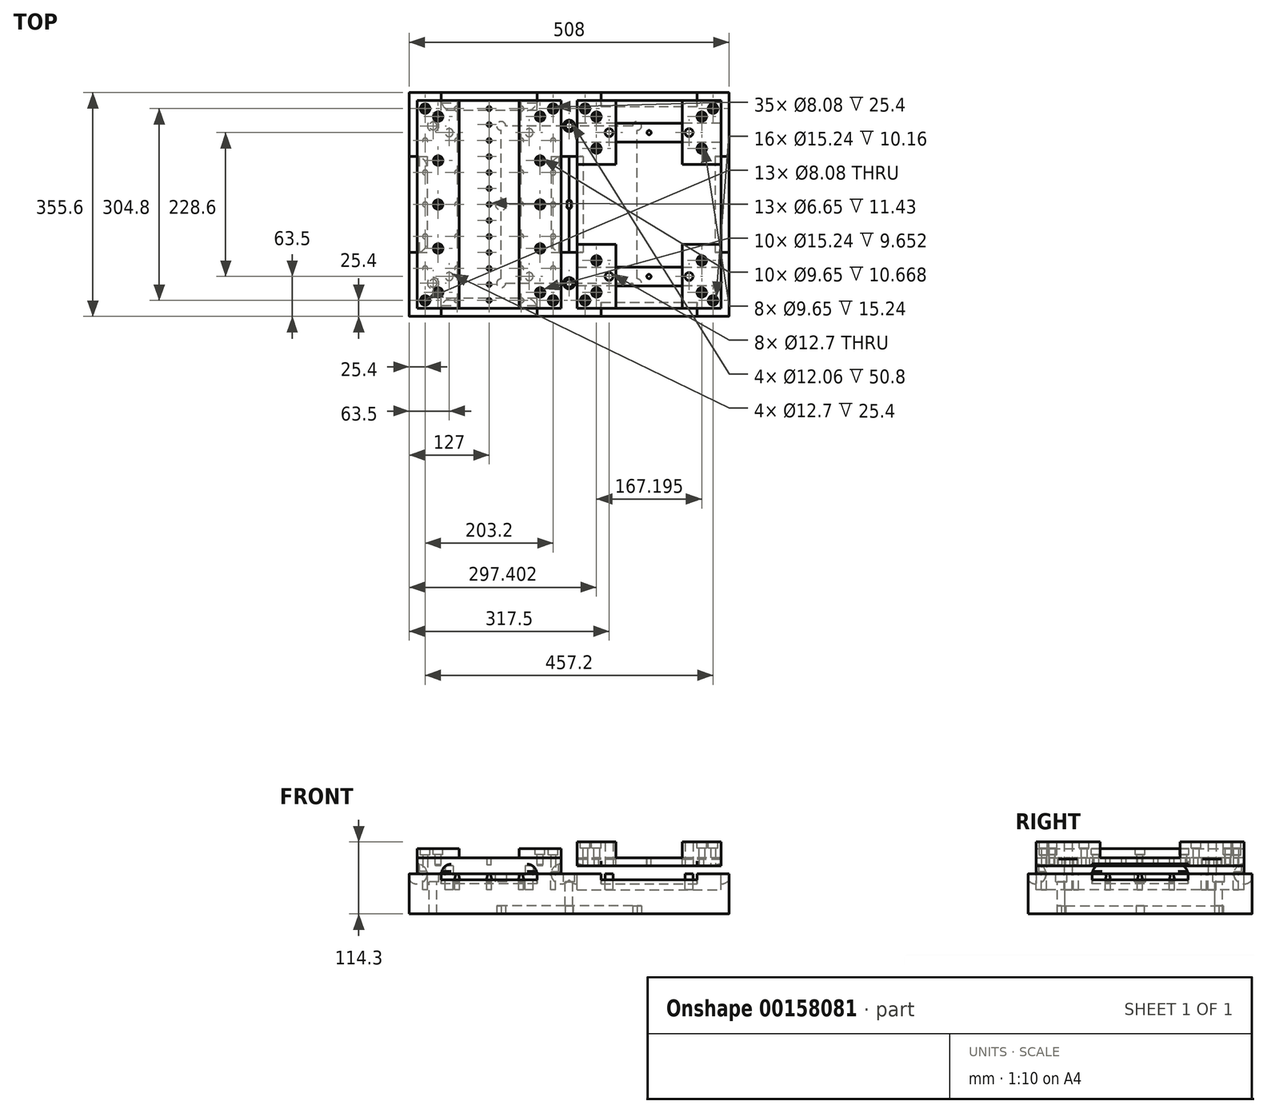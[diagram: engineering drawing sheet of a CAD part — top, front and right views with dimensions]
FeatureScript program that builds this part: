
annotation { "Feature Type Name" : "Feature", "Feature Type Description" : "" }
export const myFeature = defineFeature(function(context is Context, id is Id, definition is map)
    precondition{}
    {
        {
            var Q0;
            Q0=qCreatedBy(makeId("Top.planeOp"),FACE);
            var sketch = newSketch(context, id + "F0", { "sketchPlane" : qUnion([Q0])});
            skLineSegment(sketch, "E0.bottom", {"start": v(253.62, -177.8) * mm, "end": v(-253.62, -177.8) * mm});
            skLineSegment(sketch, "E0.top", {"start": v(253.62, 177.8) * mm, "end": v(-253.62, 177.8) * mm});
            skLineSegment(sketch, "E0.left", {"start": v(254, -177.42) * mm, "end": v(254, 177.42) * mm});
            skLineSegment(sketch, "E0.right", {"start": v(-254, -177.42) * mm, "end": v(-254, 177.42) * mm});
            skPoint(sketch, "E0.middle", {"position": v(0, 0) * mm});
            skPoint(sketch, "E1.visualSharp", {"position": v(-254, 177.8) * mm});
            skArc(sketch, "E1.filletArc", {"start": v(-253.62, 177.8) * mm, "mid": v(-253.89, 177.69) * mm, "end": v(-254, 177.42) * mm});
            skPoint(sketch, "E2.visualSharp", {"position": v(254, 177.8) * mm});
            skArc(sketch, "E2.filletArc", {"start": v(254, 177.42) * mm, "mid": v(253.89, 177.69) * mm, "end": v(253.62, 177.8) * mm});
            skPoint(sketch, "E3.visualSharp", {"position": v(254, -177.8) * mm});
            skArc(sketch, "E3.filletArc", {"start": v(253.62, -177.8) * mm, "mid": v(253.89, -177.69) * mm, "end": v(254, -177.42) * mm});
            skPoint(sketch, "E4.visualSharp", {"position": v(-254, -177.8) * mm});
            skArc(sketch, "E4.filletArc", {"start": v(-254, -177.42) * mm, "mid": v(-253.89, -177.69) * mm, "end": v(-253.62, -177.8) * mm});
            skSolve(sketch);
        }
        {
            var Q0;
            Q0 = qSketchRegion(id + "F0", true);
            extrude(context, id + "F1", {"entities" : qUnion([Q0]), "oppositeDirection" : true, "depth" : 63.5 * mm});
        }
        {
            var Q0;
            Q0=makeQuery(id+"F1.opExtrude","CAP_FACE",FACE,{"disambiguationData":[OSD([sQuery(id+"F0.wireOp",EDGE,"E0.bottom"),sQuery(id+"F0.wireOp",EDGE,"E0.top"),sQuery(id+"F0.wireOp",EDGE,"E0.left"),sQuery(id+"F0.wireOp",EDGE,"E0.right")])],"isStart":true});
            var sketch = newSketch(context, id + "F2", { "sketchPlane" : qUnion([Q0])});
            skLineSegment(sketch, "E5", {"start": v(254, 0) * mm, "end": v(-254, 0) * mm});
            skLineSegment(sketch, "E6", {"start": v(0, 0) * mm, "end": v(0, -125) * mm});
            skLineSegment(sketch, "E7", {"start": v(254, -125) * mm, "end": v(-254, -125) * mm});
            skLineSegment(sketch, "E8.MirrorCS", {"start": v(-254, 0) * mm, "end": v(254, 0) * mm});
            skLineSegment(sketch, "E9.MirrorCS", {"start": v(0, 0) * mm, "end": v(0, 125) * mm});
            skLineSegment(sketch, "E10", {"start": v(254, 125) * mm, "end": v(-254, 125) * mm});
            skLineSegment(sketch, "E11", {"start": v(254, -125) * mm, "end": v(215.9, -125) * mm});
            skLineSegment(sketch, "E12", {"start": v(254, 0) * mm, "end": v(215.9, 0) * mm});
            skLineSegment(sketch, "E13", {"start": v(254, 125) * mm, "end": v(215.9, 125) * mm});
            skLineSegment(sketch, "E14", {"start": v(215.9, 0) * mm, "end": v(0, 0) * mm});
            skLineSegment(sketch, "E15", {"start": v(0, 0) * mm, "end": v(-215.9, 0) * mm});
            skCircle(sketch, "E16", {"center": v(215.9, -125) * mm, "radius": 6.03 * mm});
            skCircle(sketch, "E17", {"center": v(215.9, 125) * mm, "radius": 6.03 * mm});
            skCircle(sketch, "E18.1.0.0", {"center": v(0, 125) * mm, "radius": 6.03 * mm});
            skCircle(sketch, "E18.1.0.1", {"center": v(0, -125) * mm, "radius": 6.03 * mm});
            skCircle(sketch, "E18.2.0.0", {"center": v(-215.9, 125) * mm, "radius": 6.03 * mm});
            skCircle(sketch, "E18.2.0.1", {"center": v(-215.9, -125) * mm, "radius": 6.03 * mm});
            skLineSegment(sketch, "E18.direction1", {"start": v(215.9, 125) * mm, "end": v(0, 125) * mm, "construction": true});
            skCircle(sketch, "E19", {"center": v(107.95, 0) * mm, "radius": 6.03 * mm});
            skCircle(sketch, "E20", {"center": v(-107.95, 0) * mm, "radius": 6.03 * mm});
            skCircle(sketch, "E21", {"center": v(0, 0) * mm, "radius": 6.35 * mm});
            skSolve(sketch);
        }
        {
            var Q0;
            {var subQ0=sQuery(id+"F2.wireOp",EDGE,"E11");var subQ1=sQuery(id+"F2.wireOp",EDGE,"E7");var subQ2=makeQuery(id+"F2.imprint","INTERSECT",VERTEX,{"derivedFrom":[subQ1,subQ0]});Q0=makeQuery(id+"F2.imprint","IMPRINT",FACE,{"disambiguationData":[TD([[makeQuery(id+"F2.imprint","IMPRINT",EDGE,{"disambiguationData":[TD([[subQ2,-1.0]])],"derivedFrom":subQ1}),-1.0]])]});}
            var Q1;
            {var subQ0=sQuery(id+"F2.wireOp",EDGE,"E11");var subQ1=sQuery(id+"F2.wireOp",EDGE,"E7");var subQ2=makeQuery(id+"F2.imprint","INTERSECT",VERTEX,{"derivedFrom":[subQ1,subQ0]});Q1=makeQuery(id+"F2.imprint","IMPRINT",FACE,{"disambiguationData":[TD([[makeQuery(id+"F2.imprint","IMPRINT",EDGE,{"disambiguationData":[TD([[subQ2,-1.0]])],"derivedFrom":subQ1}),1.0]])]});}
            var Q2;
            {var subQ0=sQuery(id+"F2.wireOp",EDGE,"E18.2.0.1");var subQ1=sQuery(id+"F2.wireOp",EDGE,"E7");var subQ2=makeQuery(id+"F2.imprint","INTERSECT",VERTEX,{"disambiguationData":[OD(0.0)],"derivedFrom":[subQ1,subQ0]});Q2=makeQuery(id+"F2.imprint","IMPRINT",FACE,{"disambiguationData":[TD([[makeQuery(id+"F2.imprint","IMPRINT",EDGE,{"disambiguationData":[TD([[subQ2,-1.0]])],"derivedFrom":subQ1}),-1.0]])]});}
            var Q3;
            {var subQ0=sQuery(id+"F2.wireOp",EDGE,"E18.2.0.1");var subQ1=sQuery(id+"F2.wireOp",EDGE,"E7");var subQ2=makeQuery(id+"F2.imprint","INTERSECT",VERTEX,{"disambiguationData":[OD(0.0)],"derivedFrom":[subQ1,subQ0]});Q3=makeQuery(id+"F2.imprint","IMPRINT",FACE,{"disambiguationData":[TD([[makeQuery(id+"F2.imprint","IMPRINT",EDGE,{"disambiguationData":[TD([[subQ2,-1.0]])],"derivedFrom":subQ1}),1.0]])]});}
            var Q4;
            {var subQ0=sQuery(id+"F2.wireOp",EDGE,"E13");var subQ1=sQuery(id+"F2.wireOp",EDGE,"E10");var subQ2=makeQuery(id+"F2.imprint","INTERSECT",VERTEX,{"derivedFrom":[subQ1,subQ0]});Q4=makeQuery(id+"F2.imprint","IMPRINT",FACE,{"disambiguationData":[TD([[makeQuery(id+"F2.imprint","IMPRINT",EDGE,{"disambiguationData":[TD([[subQ2,-1.0]])],"derivedFrom":subQ1}),-1.0]])]});}
            var Q5;
            {var subQ0=sQuery(id+"F2.wireOp",EDGE,"E13");var subQ1=sQuery(id+"F2.wireOp",EDGE,"E10");var subQ2=makeQuery(id+"F2.imprint","INTERSECT",VERTEX,{"derivedFrom":[subQ1,subQ0]});Q5=makeQuery(id+"F2.imprint","IMPRINT",FACE,{"disambiguationData":[TD([[makeQuery(id+"F2.imprint","IMPRINT",EDGE,{"disambiguationData":[TD([[subQ2,-1.0]])],"derivedFrom":subQ1}),1.0]])]});}
            var Q6;
            {var subQ0=sQuery(id+"F2.wireOp",EDGE,"E18.2.0.0");var subQ1=sQuery(id+"F2.wireOp",EDGE,"E10");var subQ2=makeQuery(id+"F2.imprint","INTERSECT",VERTEX,{"disambiguationData":[OD(0.0)],"derivedFrom":[subQ1,subQ0]});Q6=makeQuery(id+"F2.imprint","IMPRINT",FACE,{"disambiguationData":[TD([[makeQuery(id+"F2.imprint","IMPRINT",EDGE,{"disambiguationData":[TD([[subQ2,-1.0]])],"derivedFrom":subQ1}),-1.0]])]});}
            var Q7;
            {var subQ0=sQuery(id+"F2.wireOp",EDGE,"E18.2.0.0");var subQ1=sQuery(id+"F2.wireOp",EDGE,"E10");var subQ2=makeQuery(id+"F2.imprint","INTERSECT",VERTEX,{"disambiguationData":[OD(0.0)],"derivedFrom":[subQ1,subQ0]});Q7=makeQuery(id+"F2.imprint","IMPRINT",FACE,{"disambiguationData":[TD([[makeQuery(id+"F2.imprint","IMPRINT",EDGE,{"disambiguationData":[TD([[subQ2,-1.0]])],"derivedFrom":subQ1}),1.0]])]});}
            var Q8;
            {var subQ0=sQuery(id+"F2.wireOp",EDGE,"E19");var subQ1=sQuery(id+"F2.wireOp",EDGE,"E14");var subQ2=makeQuery(id+"F2.imprint","INTERSECT",VERTEX,{"disambiguationData":[OD(0.0)],"derivedFrom":[subQ1,subQ0]});Q8=makeQuery(id+"F2.imprint","IMPRINT",FACE,{"disambiguationData":[TD([[makeQuery(id+"F2.imprint","IMPRINT",EDGE,{"disambiguationData":[TD([[subQ2,-1.0]])],"derivedFrom":subQ1}),-1.0]])]});}
            var Q9;
            {var subQ0=sQuery(id+"F2.wireOp",EDGE,"E19");var subQ1=sQuery(id+"F2.wireOp",EDGE,"E14");var subQ2=makeQuery(id+"F2.imprint","INTERSECT",VERTEX,{"disambiguationData":[OD(0.0)],"derivedFrom":[subQ1,subQ0]});Q9=makeQuery(id+"F2.imprint","IMPRINT",FACE,{"disambiguationData":[TD([[makeQuery(id+"F2.imprint","IMPRINT",EDGE,{"disambiguationData":[TD([[subQ2,-1.0]])],"derivedFrom":subQ1}),1.0]])]});}
            var Q10;
            {var subQ0=sQuery(id+"F2.wireOp",EDGE,"E20");var subQ1=sQuery(id+"F2.wireOp",EDGE,"E15");var subQ2=makeQuery(id+"F2.imprint","INTERSECT",VERTEX,{"disambiguationData":[OD(0.0)],"derivedFrom":[subQ1,subQ0]});Q10=makeQuery(id+"F2.imprint","IMPRINT",FACE,{"disambiguationData":[TD([[makeQuery(id+"F2.imprint","IMPRINT",EDGE,{"disambiguationData":[TD([[subQ2,-1.0]])],"derivedFrom":subQ1}),-1.0]])]});}
            var Q11;
            {var subQ0=sQuery(id+"F2.wireOp",EDGE,"E20");var subQ1=sQuery(id+"F2.wireOp",EDGE,"E15");var subQ2=makeQuery(id+"F2.imprint","INTERSECT",VERTEX,{"disambiguationData":[OD(0.0)],"derivedFrom":[subQ1,subQ0]});Q11=makeQuery(id+"F2.imprint","IMPRINT",FACE,{"disambiguationData":[TD([[makeQuery(id+"F2.imprint","IMPRINT",EDGE,{"disambiguationData":[TD([[subQ2,-1.0]])],"derivedFrom":subQ1}),1.0]])]});}
            var Q12;
            {var subQ0=sQuery(id+"F2.wireOp",EDGE,"E7");var subQ1=sQuery(id+"F2.wireOp",EDGE,"E6");var subQ2=makeQuery(id+"F2.imprint","INTERSECT",VERTEX,{"derivedFrom":[subQ1,subQ0]});Q12=makeQuery(id+"F2.imprint","IMPRINT",FACE,{"disambiguationData":[TD([[makeQuery(id+"F2.imprint","IMPRINT",EDGE,{"disambiguationData":[TD([[subQ2,1.0]])],"derivedFrom":subQ1}),1.0]])]});}
            var Q13;
            {var subQ0=sQuery(id+"F2.wireOp",EDGE,"E7");var subQ1=sQuery(id+"F2.wireOp",EDGE,"E6");var subQ2=makeQuery(id+"F2.imprint","INTERSECT",VERTEX,{"derivedFrom":[subQ1,subQ0]});Q13=makeQuery(id+"F2.imprint","IMPRINT",FACE,{"disambiguationData":[TD([[makeQuery(id+"F2.imprint","IMPRINT",EDGE,{"disambiguationData":[TD([[subQ2,1.0]])],"derivedFrom":subQ1}),-1.0]])]});}
            var Q14;
            {var subQ0=sQuery(id+"F2.wireOp",EDGE,"E7");var subQ1=makeQuery(id+"F2.imprint","INTERSECT",VERTEX,{"derivedFrom":[sQuery(id+"F2.wireOp",EDGE,"E6"),subQ0]});Q14=makeQuery(id+"F2.imprint","IMPRINT",FACE,{"disambiguationData":[TD([[makeQuery(id+"F2.imprint","IMPRINT",EDGE,{"disambiguationData":[TD([[subQ1,1.0]])],"derivedFrom":subQ0}),1.0]])]});}
            var Q15;
            {var subQ0=sQuery(id+"F2.wireOp",EDGE,"E10");var subQ1=sQuery(id+"F2.wireOp",EDGE,"E9.MirrorCS");var subQ2=makeQuery(id+"F2.imprint","INTERSECT",VERTEX,{"derivedFrom":[subQ1,subQ0]});Q15=makeQuery(id+"F2.imprint","IMPRINT",FACE,{"disambiguationData":[TD([[makeQuery(id+"F2.imprint","IMPRINT",EDGE,{"disambiguationData":[TD([[subQ2,1.0]])],"derivedFrom":subQ1}),-1.0]])]});}
            var Q16;
            {var subQ0=sQuery(id+"F2.wireOp",EDGE,"E10");var subQ1=sQuery(id+"F2.wireOp",EDGE,"E9.MirrorCS");var subQ2=makeQuery(id+"F2.imprint","INTERSECT",VERTEX,{"derivedFrom":[subQ1,subQ0]});Q16=makeQuery(id+"F2.imprint","IMPRINT",FACE,{"disambiguationData":[TD([[makeQuery(id+"F2.imprint","IMPRINT",EDGE,{"disambiguationData":[TD([[subQ2,1.0]])],"derivedFrom":subQ1}),1.0]])]});}
            var Q17;
            {var subQ0=sQuery(id+"F2.wireOp",EDGE,"E10");var subQ1=makeQuery(id+"F2.imprint","INTERSECT",VERTEX,{"derivedFrom":[sQuery(id+"F2.wireOp",EDGE,"E9.MirrorCS"),subQ0]});Q17=makeQuery(id+"F2.imprint","IMPRINT",FACE,{"disambiguationData":[TD([[makeQuery(id+"F2.imprint","IMPRINT",EDGE,{"disambiguationData":[TD([[subQ1,1.0]])],"derivedFrom":subQ0}),-1.0]])]});}
            extrude(context, id + "F3", {"entities" : qUnion([Q0, Q1, Q2, Q3, Q4, Q5, Q6, Q7, Q8, Q9, Q10, Q11, Q12, Q13, Q14, Q15, Q16, Q17]), "operationType" : NewBodyOperationType.REMOVE, "oppositeDirection" : true, "depth" : 76.2 * mm});
        }
        {
            var Q0;
            {var subQ1=sQuery(id+"F2.wireOp",EDGE,"E6");var subQ3=sQuery(id+"F2.wireOp",EDGE,"E21");var subQ4=makeQuery(id+"F2.imprint","INTERSECT",VERTEX,{"derivedFrom":[subQ1,subQ3]});Q0=makeQuery(id+"F2.imprint","IMPRINT",FACE,{"disambiguationData":[TD([[makeQuery(id+"F2.imprint","IMPRINT",EDGE,{"disambiguationData":[TD([[subQ4,1.0]])],"derivedFrom":subQ3}),1.0]])]});}
            var Q1;
            {var subQ1=sQuery(id+"F2.wireOp",EDGE,"E6");var subQ3=sQuery(id+"F2.wireOp",EDGE,"E21");var subQ4=makeQuery(id+"F2.imprint","INTERSECT",VERTEX,{"derivedFrom":[subQ1,subQ3]});Q1=makeQuery(id+"F2.imprint","IMPRINT",FACE,{"disambiguationData":[TD([[makeQuery(id+"F2.imprint","IMPRINT",EDGE,{"disambiguationData":[TD([[subQ4,-1.0]])],"derivedFrom":subQ3}),1.0]])]});}
            var Q2;
            {var subQ1=sQuery(id+"F2.wireOp",EDGE,"E9.MirrorCS");var subQ3=sQuery(id+"F2.wireOp",EDGE,"E21");var subQ4=makeQuery(id+"F2.imprint","INTERSECT",VERTEX,{"derivedFrom":[subQ1,subQ3]});Q2=makeQuery(id+"F2.imprint","IMPRINT",FACE,{"disambiguationData":[TD([[makeQuery(id+"F2.imprint","IMPRINT",EDGE,{"disambiguationData":[TD([[subQ4,1.0]])],"derivedFrom":subQ3}),1.0]])]});}
            var Q3;
            {var subQ1=sQuery(id+"F2.wireOp",EDGE,"E9.MirrorCS");var subQ3=sQuery(id+"F2.wireOp",EDGE,"E21");var subQ4=makeQuery(id+"F2.imprint","INTERSECT",VERTEX,{"derivedFrom":[subQ1,subQ3]});Q3=makeQuery(id+"F2.imprint","IMPRINT",FACE,{"disambiguationData":[TD([[makeQuery(id+"F2.imprint","IMPRINT",EDGE,{"disambiguationData":[TD([[subQ4,-1.0]])],"derivedFrom":subQ3}),1.0]])]});}
            extrude(context, id + "F4", {"entities" : qUnion([Q0, Q1, Q2, Q3]), "operationType" : NewBodyOperationType.REMOVE, "oppositeDirection" : true, "depth" : 12.7 * mm});
        }
        {
            var Q0;
            Q0=makeQuery(id+"F1.opExtrude","CAP_FACE",FACE,{"disambiguationData":[OSD([sQuery(id+"F0.wireOp",EDGE,"E0.bottom"),sQuery(id+"F0.wireOp",EDGE,"E0.top"),sQuery(id+"F0.wireOp",EDGE,"E0.left"),sQuery(id+"F0.wireOp",EDGE,"E0.right")])],"isStart":true});
            var sketch = newSketch(context, id + "F5", { "sketchPlane" : qUnion([Q0])});
            skCircle(sketch, "E22", {"center": v(215.9, -125) * mm, "radius": 9.02 * mm});
            skCircle(sketch, "E23", {"center": v(0, -125) * mm, "radius": 9.02 * mm});
            skCircle(sketch, "E24", {"center": v(107.95, 0) * mm, "radius": 9.02 * mm});
            skCircle(sketch, "E25", {"center": v(215.9, 125) * mm, "radius": 9.02 * mm});
            skCircle(sketch, "E26", {"center": v(0, 125) * mm, "radius": 9.02 * mm});
            skCircle(sketch, "E27", {"center": v(-215.9, 125) * mm, "radius": 9.02 * mm});
            skCircle(sketch, "E28", {"center": v(-107.95, 0) * mm, "radius": 9.02 * mm});
            skCircle(sketch, "E29", {"center": v(-215.9, -125) * mm, "radius": 9.02 * mm});
            skSolve(sketch);
        }
        {
            var Q0;
            Q0 = qSketchRegion(id + "F5", true);
            extrude(context, id + "F6", {"entities" : qUnion([Q0]), "operationType" : NewBodyOperationType.REMOVE, "oppositeDirection" : true, "depth" : 12.7 * mm});
        }
        {
            var Q0;
            Q0=makeQuery(id+"F1.opExtrude","CAP_FACE",FACE,{"disambiguationData":[OSD([sQuery(id+"F0.wireOp",EDGE,"E0.bottom"),sQuery(id+"F0.wireOp",EDGE,"E0.top"),sQuery(id+"F0.wireOp",EDGE,"E0.left"),sQuery(id+"F0.wireOp",EDGE,"E0.right"),sQuery(id+"F0.wireOp",EDGE,"E1.filletArc"),sQuery(id+"F0.wireOp",EDGE,"E2.filletArc"),sQuery(id+"F0.wireOp",EDGE,"E3.filletArc"),sQuery(id+"F0.wireOp",EDGE,"E4.filletArc")])],"isStart":false});
            var sketch = newSketch(context, id + "F7", { "sketchPlane" : qUnion([Q0])});
            skLineSegment(sketch, "E30", {"start": v(-215.9, 125) * mm, "end": v(215.9, 125) * mm});
            skLineSegment(sketch, "E31", {"start": v(215.9, 125) * mm, "end": v(215.9, -125) * mm});
            skLineSegment(sketch, "E32", {"start": v(215.9, -125) * mm, "end": v(-215.9, -125) * mm});
            skLineSegment(sketch, "E33", {"start": v(-215.9, -125) * mm, "end": v(-215.9, 125) * mm});
            skLineSegment(sketch, "E34", {"start": v(-215.9, 0) * mm, "end": v(215.9, 0) * mm});
            skLineSegment(sketch, "E35", {"start": v(-107.95, 0) * mm, "end": v(-107.95, 125) * mm});
            skLineSegment(sketch, "E36", {"start": v(-107.95, 0) * mm, "end": v(-107.95, -125) * mm});
            skLineSegment(sketch, "E37", {"start": v(107.95, 0) * mm, "end": v(107.95, 125) * mm});
            skLineSegment(sketch, "E38", {"start": v(107.95, 0) * mm, "end": v(107.95, -125) * mm});
            skCircle(sketch, "E39", {"center": v(-107.95, -125) * mm, "radius": 7 * mm});
            skCircle(sketch, "E40", {"center": v(-107.95, 125) * mm, "radius": 7 * mm});
            skCircle(sketch, "E41", {"center": v(107.95, 125) * mm, "radius": 7 * mm});
            skCircle(sketch, "E42", {"center": v(107.95, -125) * mm, "radius": 7 * mm});
            skCircle(sketch, "E43", {"center": v(0, 0) * mm, "radius": 6.35 * mm});
            skSolve(sketch);
        }
        {
            var Q0;
            {var subQ0=sQuery(id+"F7.wireOp",EDGE,"E30");var subQ1=makeQuery(id+"F7.imprint","INTERSECT",VERTEX,{"derivedFrom":[subQ0,sQuery(id+"F7.wireOp",EDGE,"E35")]});Q0=makeQuery(id+"F7.imprint","IMPRINT",FACE,{"disambiguationData":[TD([[makeQuery(id+"F7.imprint","IMPRINT",EDGE,{"disambiguationData":[TD([[subQ1,1.0]])],"derivedFrom":subQ0}),1.0]])]});}
            var Q1;
            {var subQ0=sQuery(id+"F7.wireOp",EDGE,"E35");var subQ1=sQuery(id+"F7.wireOp",EDGE,"E30");var subQ2=makeQuery(id+"F7.imprint","INTERSECT",VERTEX,{"derivedFrom":[subQ1,subQ0]});Q1=makeQuery(id+"F7.imprint","IMPRINT",FACE,{"disambiguationData":[TD([[makeQuery(id+"F7.imprint","IMPRINT",EDGE,{"disambiguationData":[TD([[subQ2,1.0]])],"derivedFrom":subQ1}),-1.0]])]});}
            var Q2;
            {var subQ0=sQuery(id+"F7.wireOp",EDGE,"E35");var subQ1=sQuery(id+"F7.wireOp",EDGE,"E30");var subQ2=makeQuery(id+"F7.imprint","INTERSECT",VERTEX,{"derivedFrom":[subQ1,subQ0]});Q2=makeQuery(id+"F7.imprint","IMPRINT",FACE,{"disambiguationData":[TD([[makeQuery(id+"F7.imprint","IMPRINT",EDGE,{"disambiguationData":[TD([[subQ2,-1.0]])],"derivedFrom":subQ1}),-1.0]])]});}
            var Q3;
            {var subQ0=sQuery(id+"F7.wireOp",EDGE,"E30");var subQ1=makeQuery(id+"F7.imprint","INTERSECT",VERTEX,{"derivedFrom":[subQ0,sQuery(id+"F7.wireOp",EDGE,"E37")]});Q3=makeQuery(id+"F7.imprint","IMPRINT",FACE,{"disambiguationData":[TD([[makeQuery(id+"F7.imprint","IMPRINT",EDGE,{"disambiguationData":[TD([[subQ1,1.0]])],"derivedFrom":subQ0}),1.0]])]});}
            var Q4;
            {var subQ0=sQuery(id+"F7.wireOp",EDGE,"E37");var subQ1=sQuery(id+"F7.wireOp",EDGE,"E30");var subQ2=makeQuery(id+"F7.imprint","INTERSECT",VERTEX,{"derivedFrom":[subQ1,subQ0]});Q4=makeQuery(id+"F7.imprint","IMPRINT",FACE,{"disambiguationData":[TD([[makeQuery(id+"F7.imprint","IMPRINT",EDGE,{"disambiguationData":[TD([[subQ2,1.0]])],"derivedFrom":subQ1}),-1.0]])]});}
            var Q5;
            {var subQ0=sQuery(id+"F7.wireOp",EDGE,"E37");var subQ1=sQuery(id+"F7.wireOp",EDGE,"E30");var subQ2=makeQuery(id+"F7.imprint","INTERSECT",VERTEX,{"derivedFrom":[subQ1,subQ0]});Q5=makeQuery(id+"F7.imprint","IMPRINT",FACE,{"disambiguationData":[TD([[makeQuery(id+"F7.imprint","IMPRINT",EDGE,{"disambiguationData":[TD([[subQ2,-1.0]])],"derivedFrom":subQ1}),-1.0]])]});}
            var Q6;
            {var subQ0=sQuery(id+"F7.wireOp",EDGE,"E32");var subQ1=makeQuery(id+"F7.imprint","INTERSECT",VERTEX,{"derivedFrom":[subQ0,sQuery(id+"F7.wireOp",EDGE,"E38")]});Q6=makeQuery(id+"F7.imprint","IMPRINT",FACE,{"disambiguationData":[TD([[makeQuery(id+"F7.imprint","IMPRINT",EDGE,{"disambiguationData":[TD([[subQ1,1.0]])],"derivedFrom":subQ0}),1.0]])]});}
            var Q7;
            {var subQ0=sQuery(id+"F7.wireOp",EDGE,"E38");var subQ1=sQuery(id+"F7.wireOp",EDGE,"E32");var subQ2=makeQuery(id+"F7.imprint","INTERSECT",VERTEX,{"derivedFrom":[subQ1,subQ0]});Q7=makeQuery(id+"F7.imprint","IMPRINT",FACE,{"disambiguationData":[TD([[makeQuery(id+"F7.imprint","IMPRINT",EDGE,{"disambiguationData":[TD([[subQ2,-1.0]])],"derivedFrom":subQ1}),-1.0]])]});}
            var Q8;
            {var subQ0=sQuery(id+"F7.wireOp",EDGE,"E38");var subQ1=sQuery(id+"F7.wireOp",EDGE,"E32");var subQ2=makeQuery(id+"F7.imprint","INTERSECT",VERTEX,{"derivedFrom":[subQ1,subQ0]});Q8=makeQuery(id+"F7.imprint","IMPRINT",FACE,{"disambiguationData":[TD([[makeQuery(id+"F7.imprint","IMPRINT",EDGE,{"disambiguationData":[TD([[subQ2,1.0]])],"derivedFrom":subQ1}),-1.0]])]});}
            var Q9;
            {var subQ0=sQuery(id+"F7.wireOp",EDGE,"E36");var subQ1=sQuery(id+"F7.wireOp",EDGE,"E32");var subQ2=makeQuery(id+"F7.imprint","INTERSECT",VERTEX,{"derivedFrom":[subQ1,subQ0]});Q9=makeQuery(id+"F7.imprint","IMPRINT",FACE,{"disambiguationData":[TD([[makeQuery(id+"F7.imprint","IMPRINT",EDGE,{"disambiguationData":[TD([[subQ2,-1.0]])],"derivedFrom":subQ1}),-1.0]])]});}
            var Q10;
            {var subQ0=sQuery(id+"F7.wireOp",EDGE,"E36");var subQ1=sQuery(id+"F7.wireOp",EDGE,"E32");var subQ2=makeQuery(id+"F7.imprint","INTERSECT",VERTEX,{"derivedFrom":[subQ1,subQ0]});Q10=makeQuery(id+"F7.imprint","IMPRINT",FACE,{"disambiguationData":[TD([[makeQuery(id+"F7.imprint","IMPRINT",EDGE,{"disambiguationData":[TD([[subQ2,1.0]])],"derivedFrom":subQ1}),-1.0]])]});}
            var Q11;
            {var subQ0=sQuery(id+"F7.wireOp",EDGE,"E32");var subQ1=makeQuery(id+"F7.imprint","INTERSECT",VERTEX,{"derivedFrom":[subQ0,sQuery(id+"F7.wireOp",EDGE,"E36")]});Q11=makeQuery(id+"F7.imprint","IMPRINT",FACE,{"disambiguationData":[TD([[makeQuery(id+"F7.imprint","IMPRINT",EDGE,{"disambiguationData":[TD([[subQ1,1.0]])],"derivedFrom":subQ0}),1.0]])]});}
            var Q12;
            {var subQ0=sQuery(id+"F7.wireOp",EDGE,"E43");var subQ1=sQuery(id+"F7.wireOp",EDGE,"E34");var subQ2=makeQuery(id+"F7.imprint","INTERSECT",VERTEX,{"disambiguationData":[OD(0.0)],"derivedFrom":[subQ1,subQ0]});Q12=makeQuery(id+"F7.imprint","IMPRINT",FACE,{"disambiguationData":[TD([[makeQuery(id+"F7.imprint","IMPRINT",EDGE,{"disambiguationData":[TD([[subQ2,-1.0]])],"derivedFrom":subQ1}),-1.0]])]});}
            var Q13;
            {var subQ0=sQuery(id+"F7.wireOp",EDGE,"E43");var subQ1=sQuery(id+"F7.wireOp",EDGE,"E34");var subQ2=makeQuery(id+"F7.imprint","INTERSECT",VERTEX,{"disambiguationData":[OD(0.0)],"derivedFrom":[subQ1,subQ0]});Q13=makeQuery(id+"F7.imprint","IMPRINT",FACE,{"disambiguationData":[TD([[makeQuery(id+"F7.imprint","IMPRINT",EDGE,{"disambiguationData":[TD([[subQ2,-1.0]])],"derivedFrom":subQ1}),1.0]])]});}
            extrude(context, id + "F8", {"entities" : qUnion([Q0, Q1, Q2, Q3, Q4, Q5, Q6, Q7, Q8, Q9, Q10, Q11, Q12, Q13]), "operationType" : NewBodyOperationType.REMOVE, "oppositeDirection" : true, "depth" : 12.7 * mm});
        }
        {
            var Q0;
            Q0=makeQuery(id+"F0.imprint","IMPRINT",FACE,{"disambiguationData":[TD([[makeQuery(id+"F0.imprint","IMPRINT",EDGE,{"derivedFrom":sQuery(id+"F0.wireOp",EDGE,"E0.bottom")}),-1.0]])]});
            var sketch = newSketch(context, id + "F9", { "sketchPlane" : qUnion([Q0])});
            skLineSegment(sketch, "E44", {"start": v(0, 0) * mm, "end": v(-254, 0) * mm});
            skLineSegment(sketch, "E45", {"start": v(-254, 177.8) * mm, "end": v(-254, 0) * mm});
            skLineSegment(sketch, "E46", {"start": v(-254, 177.8) * mm, "end": v(-228.6, 177.8) * mm});
            skLineSegment(sketch, "E47", {"start": v(-228.6, 177.8) * mm, "end": v(-228.6, 152.4) * mm});
            skCircle(sketch, "E48", {"center": v(-228.6, 152.4) * mm, "radius": 4.04 * mm});
            skCircle(sketch, "E49.0.1.0", {"center": v(-228.6, 101.6) * mm, "radius": 4.04 * mm});
            skCircle(sketch, "E49.0.2.0", {"center": v(-228.6, 50.8) * mm, "radius": 4.04 * mm});
            skCircle(sketch, "E49.0.3.0", {"center": v(-228.6, 0) * mm, "radius": 4.04 * mm});
            skCircle(sketch, "E49.0.4.0", {"center": v(-228.6, -50.8) * mm, "radius": 4.04 * mm});
            skCircle(sketch, "E49.0.5.0", {"center": v(-228.6, -101.6) * mm, "radius": 4.04 * mm});
            skCircle(sketch, "E49.0.6.0", {"center": v(-228.6, -152.4) * mm, "radius": 4.04 * mm});
            skCircle(sketch, "E49.1.0.0", {"center": v(-177.8, 152.4) * mm, "radius": 4.04 * mm});
            skCircle(sketch, "E49.1.1.0", {"center": v(-177.8, 101.6) * mm, "radius": 4.04 * mm});
            skCircle(sketch, "E49.1.2.0", {"center": v(-177.8, 50.8) * mm, "radius": 4.04 * mm});
            skCircle(sketch, "E49.1.3.0", {"center": v(-177.8, 0) * mm, "radius": 4.04 * mm});
            skCircle(sketch, "E49.1.4.0", {"center": v(-177.8, -50.8) * mm, "radius": 4.04 * mm});
            skCircle(sketch, "E49.1.5.0", {"center": v(-177.8, -101.6) * mm, "radius": 4.04 * mm});
            skCircle(sketch, "E49.1.6.0", {"center": v(-177.8, -152.4) * mm, "radius": 4.04 * mm});
            skCircle(sketch, "E49.2.0.0", {"center": v(-127, 152.4) * mm, "radius": 4.04 * mm});
            skCircle(sketch, "E49.2.1.0", {"center": v(-127, 101.6) * mm, "radius": 4.04 * mm});
            skCircle(sketch, "E49.2.2.0", {"center": v(-127, 50.8) * mm, "radius": 4.04 * mm});
            skCircle(sketch, "E49.2.3.0", {"center": v(-127, 0) * mm, "radius": 4.04 * mm});
            skCircle(sketch, "E49.2.4.0", {"center": v(-127, -50.8) * mm, "radius": 4.04 * mm});
            skCircle(sketch, "E49.2.5.0", {"center": v(-127, -101.6) * mm, "radius": 4.04 * mm});
            skCircle(sketch, "E49.2.6.0", {"center": v(-127, -152.4) * mm, "radius": 4.04 * mm});
            skCircle(sketch, "E49.3.0.0", {"center": v(-76.2, 152.4) * mm, "radius": 4.04 * mm});
            skCircle(sketch, "E49.3.1.0", {"center": v(-76.2, 101.6) * mm, "radius": 4.04 * mm});
            skCircle(sketch, "E49.3.2.0", {"center": v(-76.2, 50.8) * mm, "radius": 4.04 * mm});
            skCircle(sketch, "E49.3.3.0", {"center": v(-76.2, 0) * mm, "radius": 4.04 * mm});
            skCircle(sketch, "E49.3.4.0", {"center": v(-76.2, -50.8) * mm, "radius": 4.04 * mm});
            skCircle(sketch, "E49.3.5.0", {"center": v(-76.2, -101.6) * mm, "radius": 4.04 * mm});
            skCircle(sketch, "E49.3.6.0", {"center": v(-76.2, -152.4) * mm, "radius": 4.04 * mm});
            skCircle(sketch, "E49.4.0.0", {"center": v(-25.4, 152.4) * mm, "radius": 4.04 * mm});
            skCircle(sketch, "E49.4.1.0", {"center": v(-25.4, 101.6) * mm, "radius": 4.04 * mm});
            skCircle(sketch, "E49.4.2.0", {"center": v(-25.4, 50.8) * mm, "radius": 4.04 * mm});
            skCircle(sketch, "E49.4.3.0", {"center": v(-25.4, 0) * mm, "radius": 4.04 * mm});
            skCircle(sketch, "E49.4.4.0", {"center": v(-25.4, -50.8) * mm, "radius": 4.04 * mm});
            skCircle(sketch, "E49.4.5.0", {"center": v(-25.4, -101.6) * mm, "radius": 4.04 * mm});
            skCircle(sketch, "E49.4.6.0", {"center": v(-25.4, -152.4) * mm, "radius": 4.04 * mm});
            skCircle(sketch, "E49.5.0.0", {"center": v(25.4, 152.4) * mm, "radius": 4.04 * mm});
            skCircle(sketch, "E49.5.1.0", {"center": v(25.4, 101.6) * mm, "radius": 4.04 * mm});
            skCircle(sketch, "E49.5.2.0", {"center": v(25.4, 50.8) * mm, "radius": 4.04 * mm});
            skCircle(sketch, "E49.5.3.0", {"center": v(25.4, 0) * mm, "radius": 4.04 * mm});
            skCircle(sketch, "E49.5.4.0", {"center": v(25.4, -50.8) * mm, "radius": 4.04 * mm});
            skCircle(sketch, "E49.5.5.0", {"center": v(25.4, -101.6) * mm, "radius": 4.04 * mm});
            skCircle(sketch, "E49.5.6.0", {"center": v(25.4, -152.4) * mm, "radius": 4.04 * mm});
            skCircle(sketch, "E49.6.0.0", {"center": v(76.2, 152.4) * mm, "radius": 4.04 * mm});
            skCircle(sketch, "E49.6.1.0", {"center": v(76.2, 101.6) * mm, "radius": 4.04 * mm});
            skCircle(sketch, "E49.6.2.0", {"center": v(76.2, 50.8) * mm, "radius": 4.04 * mm});
            skCircle(sketch, "E49.6.3.0", {"center": v(76.2, 0) * mm, "radius": 4.04 * mm});
            skCircle(sketch, "E49.6.4.0", {"center": v(76.2, -50.8) * mm, "radius": 4.04 * mm});
            skCircle(sketch, "E49.6.5.0", {"center": v(76.2, -101.6) * mm, "radius": 4.04 * mm});
            skCircle(sketch, "E49.6.6.0", {"center": v(76.2, -152.4) * mm, "radius": 4.04 * mm});
            skCircle(sketch, "E49.7.0.0", {"center": v(127, 152.4) * mm, "radius": 4.04 * mm});
            skCircle(sketch, "E49.7.1.0", {"center": v(127, 101.6) * mm, "radius": 4.04 * mm});
            skCircle(sketch, "E49.7.2.0", {"center": v(127, 50.8) * mm, "radius": 4.04 * mm});
            skCircle(sketch, "E49.7.3.0", {"center": v(127, 0) * mm, "radius": 4.04 * mm});
            skCircle(sketch, "E49.7.4.0", {"center": v(127, -50.8) * mm, "radius": 4.04 * mm});
            skCircle(sketch, "E49.7.5.0", {"center": v(127, -101.6) * mm, "radius": 4.04 * mm});
            skCircle(sketch, "E49.7.6.0", {"center": v(127, -152.4) * mm, "radius": 4.04 * mm});
            skCircle(sketch, "E49.8.0.0", {"center": v(177.8, 152.4) * mm, "radius": 4.04 * mm});
            skCircle(sketch, "E49.8.1.0", {"center": v(177.8, 101.6) * mm, "radius": 4.04 * mm});
            skCircle(sketch, "E49.8.2.0", {"center": v(177.8, 50.8) * mm, "radius": 4.04 * mm});
            skCircle(sketch, "E49.8.3.0", {"center": v(177.8, 0) * mm, "radius": 4.04 * mm});
            skCircle(sketch, "E49.8.4.0", {"center": v(177.8, -50.8) * mm, "radius": 4.04 * mm});
            skCircle(sketch, "E49.8.5.0", {"center": v(177.8, -101.6) * mm, "radius": 4.04 * mm});
            skCircle(sketch, "E49.8.6.0", {"center": v(177.8, -152.4) * mm, "radius": 4.04 * mm});
            skCircle(sketch, "E49.9.0.0", {"center": v(228.6, 152.4) * mm, "radius": 4.04 * mm});
            skCircle(sketch, "E49.9.1.0", {"center": v(228.6, 101.6) * mm, "radius": 4.04 * mm});
            skCircle(sketch, "E49.9.2.0", {"center": v(228.6, 50.8) * mm, "radius": 4.04 * mm});
            skCircle(sketch, "E49.9.3.0", {"center": v(228.6, 0) * mm, "radius": 4.04 * mm});
            skCircle(sketch, "E49.9.4.0", {"center": v(228.6, -50.8) * mm, "radius": 4.04 * mm});
            skCircle(sketch, "E49.9.5.0", {"center": v(228.6, -101.6) * mm, "radius": 4.04 * mm});
            skCircle(sketch, "E49.9.6.0", {"center": v(228.6, -152.4) * mm, "radius": 4.04 * mm});
            skLineSegment(sketch, "E49.direction1", {"start": v(-228.6, 152.4) * mm, "end": v(-177.8, 152.4) * mm, "construction": true});
            skLineSegment(sketch, "E49.direction2", {"start": v(-228.6, 152.4) * mm, "end": v(-228.6, 101.6) * mm, "construction": true});
            skSolve(sketch);
        }
        {
            var Q0;
            Q0=makeQuery(id+"F9.imprint","IMPRINT",FACE,{"disambiguationData":[TD([[makeQuery(id+"F9.imprint","IMPRINT",EDGE,{"derivedFrom":sQuery(id+"F9.wireOp",EDGE,"E49.1.0.0")}),1.0]])]});
            var Q1;
            Q1=makeQuery(id+"F9.imprint","IMPRINT",FACE,{"disambiguationData":[TD([[makeQuery(id+"F9.imprint","IMPRINT",EDGE,{"derivedFrom":sQuery(id+"F9.wireOp",EDGE,"E48")}),1.0]])]});
            var Q2;
            Q2=makeQuery(id+"F9.imprint","IMPRINT",FACE,{"disambiguationData":[TD([[makeQuery(id+"F9.imprint","IMPRINT",EDGE,{"derivedFrom":sQuery(id+"F9.wireOp",EDGE,"E49.1.1.0")}),1.0]])]});
            var Q3;
            Q3=makeQuery(id+"F9.imprint","IMPRINT",FACE,{"disambiguationData":[TD([[makeQuery(id+"F9.imprint","IMPRINT",EDGE,{"derivedFrom":sQuery(id+"F9.wireOp",EDGE,"E49.0.1.0")}),1.0]])]});
            var Q4;
            Q4=makeQuery(id+"F9.imprint","IMPRINT",FACE,{"disambiguationData":[TD([[makeQuery(id+"F9.imprint","IMPRINT",EDGE,{"derivedFrom":sQuery(id+"F9.wireOp",EDGE,"E49.0.2.0")}),1.0]])]});
            var Q5;
            Q5=makeQuery(id+"F9.imprint","IMPRINT",FACE,{"disambiguationData":[TD([[makeQuery(id+"F9.imprint","IMPRINT",EDGE,{"derivedFrom":sQuery(id+"F9.wireOp",EDGE,"E49.1.2.0")}),1.0]])]});
            var Q6;
            {var subQ0=sQuery(id+"F9.wireOp",EDGE,"E49.1.3.0");var subQ1=sQuery(id+"F9.wireOp",EDGE,"E44");var subQ2=makeQuery(id+"F9.imprint","INTERSECT",VERTEX,{"disambiguationData":[OD(0.0)],"derivedFrom":[subQ1,subQ0]});Q6=makeQuery(id+"F9.imprint","IMPRINT",FACE,{"disambiguationData":[TD([[makeQuery(id+"F9.imprint","IMPRINT",EDGE,{"disambiguationData":[TD([[subQ2,1.0]])],"derivedFrom":subQ1}),-1.0]])]});}
            var Q7;
            {var subQ0=sQuery(id+"F9.wireOp",EDGE,"E49.1.3.0");var subQ1=sQuery(id+"F9.wireOp",EDGE,"E44");var subQ2=makeQuery(id+"F9.imprint","INTERSECT",VERTEX,{"disambiguationData":[OD(0.0)],"derivedFrom":[subQ1,subQ0]});Q7=makeQuery(id+"F9.imprint","IMPRINT",FACE,{"disambiguationData":[TD([[makeQuery(id+"F9.imprint","IMPRINT",EDGE,{"disambiguationData":[TD([[subQ2,1.0]])],"derivedFrom":subQ1}),1.0]])]});}
            var Q8;
            {var subQ0=sQuery(id+"F9.wireOp",EDGE,"E49.0.3.0");var subQ1=sQuery(id+"F9.wireOp",EDGE,"E44");var subQ2=makeQuery(id+"F9.imprint","INTERSECT",VERTEX,{"disambiguationData":[OD(0.0)],"derivedFrom":[subQ1,subQ0]});Q8=makeQuery(id+"F9.imprint","IMPRINT",FACE,{"disambiguationData":[TD([[makeQuery(id+"F9.imprint","IMPRINT",EDGE,{"disambiguationData":[TD([[subQ2,1.0]])],"derivedFrom":subQ1}),1.0]])]});}
            var Q9;
            {var subQ0=sQuery(id+"F9.wireOp",EDGE,"E49.0.3.0");var subQ1=sQuery(id+"F9.wireOp",EDGE,"E44");var subQ2=makeQuery(id+"F9.imprint","INTERSECT",VERTEX,{"disambiguationData":[OD(0.0)],"derivedFrom":[subQ1,subQ0]});Q9=makeQuery(id+"F9.imprint","IMPRINT",FACE,{"disambiguationData":[TD([[makeQuery(id+"F9.imprint","IMPRINT",EDGE,{"disambiguationData":[TD([[subQ2,1.0]])],"derivedFrom":subQ1}),-1.0]])]});}
            var Q10;
            {var subQ0=sQuery(id+"F9.wireOp",EDGE,"E49.2.3.0");var subQ1=sQuery(id+"F9.wireOp",EDGE,"E44");var subQ2=makeQuery(id+"F9.imprint","INTERSECT",VERTEX,{"disambiguationData":[OD(0.0)],"derivedFrom":[subQ1,subQ0]});Q10=makeQuery(id+"F9.imprint","IMPRINT",FACE,{"disambiguationData":[TD([[makeQuery(id+"F9.imprint","IMPRINT",EDGE,{"disambiguationData":[TD([[subQ2,1.0]])],"derivedFrom":subQ1}),-1.0]])]});}
            var Q11;
            {var subQ0=sQuery(id+"F9.wireOp",EDGE,"E49.2.3.0");var subQ1=sQuery(id+"F9.wireOp",EDGE,"E44");var subQ2=makeQuery(id+"F9.imprint","INTERSECT",VERTEX,{"disambiguationData":[OD(0.0)],"derivedFrom":[subQ1,subQ0]});Q11=makeQuery(id+"F9.imprint","IMPRINT",FACE,{"disambiguationData":[TD([[makeQuery(id+"F9.imprint","IMPRINT",EDGE,{"disambiguationData":[TD([[subQ2,1.0]])],"derivedFrom":subQ1}),1.0]])]});}
            var Q12;
            {var subQ0=sQuery(id+"F9.wireOp",EDGE,"E49.3.3.0");var subQ1=sQuery(id+"F9.wireOp",EDGE,"E44");var subQ2=makeQuery(id+"F9.imprint","INTERSECT",VERTEX,{"disambiguationData":[OD(0.0)],"derivedFrom":[subQ1,subQ0]});Q12=makeQuery(id+"F9.imprint","IMPRINT",FACE,{"disambiguationData":[TD([[makeQuery(id+"F9.imprint","IMPRINT",EDGE,{"disambiguationData":[TD([[subQ2,1.0]])],"derivedFrom":subQ1}),-1.0]])]});}
            var Q13;
            {var subQ0=sQuery(id+"F9.wireOp",EDGE,"E49.3.3.0");var subQ1=sQuery(id+"F9.wireOp",EDGE,"E44");var subQ2=makeQuery(id+"F9.imprint","INTERSECT",VERTEX,{"disambiguationData":[OD(0.0)],"derivedFrom":[subQ1,subQ0]});Q13=makeQuery(id+"F9.imprint","IMPRINT",FACE,{"disambiguationData":[TD([[makeQuery(id+"F9.imprint","IMPRINT",EDGE,{"disambiguationData":[TD([[subQ2,1.0]])],"derivedFrom":subQ1}),1.0]])]});}
            var Q14;
            {var subQ0=sQuery(id+"F9.wireOp",EDGE,"E49.4.3.0");var subQ1=sQuery(id+"F9.wireOp",EDGE,"E44");var subQ2=makeQuery(id+"F9.imprint","INTERSECT",VERTEX,{"disambiguationData":[OD(0.0)],"derivedFrom":[subQ1,subQ0]});Q14=makeQuery(id+"F9.imprint","IMPRINT",FACE,{"disambiguationData":[TD([[makeQuery(id+"F9.imprint","IMPRINT",EDGE,{"disambiguationData":[TD([[subQ2,1.0]])],"derivedFrom":subQ1}),1.0]])]});}
            var Q15;
            {var subQ0=sQuery(id+"F9.wireOp",EDGE,"E49.4.3.0");var subQ1=sQuery(id+"F9.wireOp",EDGE,"E44");var subQ2=makeQuery(id+"F9.imprint","INTERSECT",VERTEX,{"disambiguationData":[OD(0.0)],"derivedFrom":[subQ1,subQ0]});Q15=makeQuery(id+"F9.imprint","IMPRINT",FACE,{"disambiguationData":[TD([[makeQuery(id+"F9.imprint","IMPRINT",EDGE,{"disambiguationData":[TD([[subQ2,1.0]])],"derivedFrom":subQ1}),-1.0]])]});}
            var Q16;
            Q16=makeQuery(id+"F9.imprint","IMPRINT",FACE,{"disambiguationData":[TD([[makeQuery(id+"F9.imprint","IMPRINT",EDGE,{"derivedFrom":sQuery(id+"F9.wireOp",EDGE,"E49.3.2.0")}),1.0]])]});
            var Q17;
            Q17=makeQuery(id+"F9.imprint","IMPRINT",FACE,{"disambiguationData":[TD([[makeQuery(id+"F9.imprint","IMPRINT",EDGE,{"derivedFrom":sQuery(id+"F9.wireOp",EDGE,"E49.2.2.0")}),1.0]])]});
            var Q18;
            Q18=makeQuery(id+"F9.imprint","IMPRINT",FACE,{"disambiguationData":[TD([[makeQuery(id+"F9.imprint","IMPRINT",EDGE,{"derivedFrom":sQuery(id+"F9.wireOp",EDGE,"E49.4.2.0")}),1.0]])]});
            var Q19;
            Q19=makeQuery(id+"F9.imprint","IMPRINT",FACE,{"disambiguationData":[TD([[makeQuery(id+"F9.imprint","IMPRINT",EDGE,{"derivedFrom":sQuery(id+"F9.wireOp",EDGE,"E49.5.2.0")}),1.0]])]});
            var Q20;
            Q20=makeQuery(id+"F9.imprint","IMPRINT",FACE,{"disambiguationData":[TD([[makeQuery(id+"F9.imprint","IMPRINT",EDGE,{"derivedFrom":sQuery(id+"F9.wireOp",EDGE,"E49.6.2.0")}),1.0]])]});
            var Q21;
            Q21=makeQuery(id+"F9.imprint","IMPRINT",FACE,{"disambiguationData":[TD([[makeQuery(id+"F9.imprint","IMPRINT",EDGE,{"derivedFrom":sQuery(id+"F9.wireOp",EDGE,"E49.6.3.0")}),1.0]])]});
            var Q22;
            Q22=makeQuery(id+"F9.imprint","IMPRINT",FACE,{"disambiguationData":[TD([[makeQuery(id+"F9.imprint","IMPRINT",EDGE,{"derivedFrom":sQuery(id+"F9.wireOp",EDGE,"E49.5.3.0")}),1.0]])]});
            var Q23;
            Q23=makeQuery(id+"F9.imprint","IMPRINT",FACE,{"disambiguationData":[TD([[makeQuery(id+"F9.imprint","IMPRINT",EDGE,{"derivedFrom":sQuery(id+"F9.wireOp",EDGE,"E49.2.0.0")}),1.0]])]});
            var Q24;
            Q24=makeQuery(id+"F9.imprint","IMPRINT",FACE,{"disambiguationData":[TD([[makeQuery(id+"F9.imprint","IMPRINT",EDGE,{"derivedFrom":sQuery(id+"F9.wireOp",EDGE,"E49.3.0.0")}),1.0]])]});
            var Q25;
            Q25=makeQuery(id+"F9.imprint","IMPRINT",FACE,{"disambiguationData":[TD([[makeQuery(id+"F9.imprint","IMPRINT",EDGE,{"derivedFrom":sQuery(id+"F9.wireOp",EDGE,"E49.4.0.0")}),1.0]])]});
            var Q26;
            Q26=makeQuery(id+"F9.imprint","IMPRINT",FACE,{"disambiguationData":[TD([[makeQuery(id+"F9.imprint","IMPRINT",EDGE,{"derivedFrom":sQuery(id+"F9.wireOp",EDGE,"E49.5.0.0")}),1.0]])]});
            var Q27;
            Q27=makeQuery(id+"F9.imprint","IMPRINT",FACE,{"disambiguationData":[TD([[makeQuery(id+"F9.imprint","IMPRINT",EDGE,{"derivedFrom":sQuery(id+"F9.wireOp",EDGE,"E49.6.0.0")}),1.0]])]});
            var Q28;
            Q28=makeQuery(id+"F9.imprint","IMPRINT",FACE,{"disambiguationData":[TD([[makeQuery(id+"F9.imprint","IMPRINT",EDGE,{"derivedFrom":sQuery(id+"F9.wireOp",EDGE,"E49.7.0.0")}),1.0]])]});
            var Q29;
            Q29=makeQuery(id+"F9.imprint","IMPRINT",FACE,{"disambiguationData":[TD([[makeQuery(id+"F9.imprint","IMPRINT",EDGE,{"derivedFrom":sQuery(id+"F9.wireOp",EDGE,"E49.7.1.0")}),1.0]])]});
            var Q30;
            Q30=makeQuery(id+"F9.imprint","IMPRINT",FACE,{"disambiguationData":[TD([[makeQuery(id+"F9.imprint","IMPRINT",EDGE,{"derivedFrom":sQuery(id+"F9.wireOp",EDGE,"E49.6.1.0")}),1.0]])]});
            var Q31;
            Q31=makeQuery(id+"F9.imprint","IMPRINT",FACE,{"disambiguationData":[TD([[makeQuery(id+"F9.imprint","IMPRINT",EDGE,{"derivedFrom":sQuery(id+"F9.wireOp",EDGE,"E49.5.1.0")}),1.0]])]});
            var Q32;
            Q32=makeQuery(id+"F9.imprint","IMPRINT",FACE,{"disambiguationData":[TD([[makeQuery(id+"F9.imprint","IMPRINT",EDGE,{"derivedFrom":sQuery(id+"F9.wireOp",EDGE,"E49.4.1.0")}),1.0]])]});
            var Q33;
            Q33=makeQuery(id+"F9.imprint","IMPRINT",FACE,{"disambiguationData":[TD([[makeQuery(id+"F9.imprint","IMPRINT",EDGE,{"derivedFrom":sQuery(id+"F9.wireOp",EDGE,"E49.3.1.0")}),1.0]])]});
            var Q34;
            Q34=makeQuery(id+"F9.imprint","IMPRINT",FACE,{"disambiguationData":[TD([[makeQuery(id+"F9.imprint","IMPRINT",EDGE,{"derivedFrom":sQuery(id+"F9.wireOp",EDGE,"E49.2.1.0")}),1.0]])]});
            var Q35;
            Q35=makeQuery(id+"F9.imprint","IMPRINT",FACE,{"disambiguationData":[TD([[makeQuery(id+"F9.imprint","IMPRINT",EDGE,{"derivedFrom":sQuery(id+"F9.wireOp",EDGE,"E49.8.0.0")}),1.0]])]});
            var Q36;
            Q36=makeQuery(id+"F9.imprint","IMPRINT",FACE,{"disambiguationData":[TD([[makeQuery(id+"F9.imprint","IMPRINT",EDGE,{"derivedFrom":sQuery(id+"F9.wireOp",EDGE,"E49.9.0.0")}),1.0]])]});
            var Q37;
            Q37=makeQuery(id+"F9.imprint","IMPRINT",FACE,{"disambiguationData":[TD([[makeQuery(id+"F9.imprint","IMPRINT",EDGE,{"derivedFrom":sQuery(id+"F9.wireOp",EDGE,"E49.9.1.0")}),1.0]])]});
            var Q38;
            Q38=makeQuery(id+"F9.imprint","IMPRINT",FACE,{"disambiguationData":[TD([[makeQuery(id+"F9.imprint","IMPRINT",EDGE,{"derivedFrom":sQuery(id+"F9.wireOp",EDGE,"E49.8.1.0")}),1.0]])]});
            var Q39;
            Q39=makeQuery(id+"F9.imprint","IMPRINT",FACE,{"disambiguationData":[TD([[makeQuery(id+"F9.imprint","IMPRINT",EDGE,{"derivedFrom":sQuery(id+"F9.wireOp",EDGE,"E49.7.2.0")}),1.0]])]});
            var Q40;
            Q40=makeQuery(id+"F9.imprint","IMPRINT",FACE,{"disambiguationData":[TD([[makeQuery(id+"F9.imprint","IMPRINT",EDGE,{"derivedFrom":sQuery(id+"F9.wireOp",EDGE,"E49.8.2.0")}),1.0]])]});
            var Q41;
            Q41=makeQuery(id+"F9.imprint","IMPRINT",FACE,{"disambiguationData":[TD([[makeQuery(id+"F9.imprint","IMPRINT",EDGE,{"derivedFrom":sQuery(id+"F9.wireOp",EDGE,"E49.9.2.0")}),1.0]])]});
            var Q42;
            Q42=makeQuery(id+"F9.imprint","IMPRINT",FACE,{"disambiguationData":[TD([[makeQuery(id+"F9.imprint","IMPRINT",EDGE,{"derivedFrom":sQuery(id+"F9.wireOp",EDGE,"E49.9.3.0")}),1.0]])]});
            var Q43;
            Q43=makeQuery(id+"F9.imprint","IMPRINT",FACE,{"disambiguationData":[TD([[makeQuery(id+"F9.imprint","IMPRINT",EDGE,{"derivedFrom":sQuery(id+"F9.wireOp",EDGE,"E49.8.3.0")}),1.0]])]});
            var Q44;
            Q44=makeQuery(id+"F9.imprint","IMPRINT",FACE,{"disambiguationData":[TD([[makeQuery(id+"F9.imprint","IMPRINT",EDGE,{"derivedFrom":sQuery(id+"F9.wireOp",EDGE,"E49.7.3.0")}),1.0]])]});
            var Q45;
            Q45=makeQuery(id+"F9.imprint","IMPRINT",FACE,{"disambiguationData":[TD([[makeQuery(id+"F9.imprint","IMPRINT",EDGE,{"derivedFrom":sQuery(id+"F9.wireOp",EDGE,"E49.9.4.0")}),1.0]])]});
            var Q46;
            Q46=makeQuery(id+"F9.imprint","IMPRINT",FACE,{"disambiguationData":[TD([[makeQuery(id+"F9.imprint","IMPRINT",EDGE,{"derivedFrom":sQuery(id+"F9.wireOp",EDGE,"E49.8.4.0")}),1.0]])]});
            var Q47;
            Q47=makeQuery(id+"F9.imprint","IMPRINT",FACE,{"disambiguationData":[TD([[makeQuery(id+"F9.imprint","IMPRINT",EDGE,{"derivedFrom":sQuery(id+"F9.wireOp",EDGE,"E49.7.4.0")}),1.0]])]});
            var Q48;
            Q48=makeQuery(id+"F9.imprint","IMPRINT",FACE,{"disambiguationData":[TD([[makeQuery(id+"F9.imprint","IMPRINT",EDGE,{"derivedFrom":sQuery(id+"F9.wireOp",EDGE,"E49.6.4.0")}),1.0]])]});
            var Q49;
            Q49=makeQuery(id+"F9.imprint","IMPRINT",FACE,{"disambiguationData":[TD([[makeQuery(id+"F9.imprint","IMPRINT",EDGE,{"derivedFrom":sQuery(id+"F9.wireOp",EDGE,"E49.5.4.0")}),1.0]])]});
            var Q50;
            Q50=makeQuery(id+"F9.imprint","IMPRINT",FACE,{"disambiguationData":[TD([[makeQuery(id+"F9.imprint","IMPRINT",EDGE,{"derivedFrom":sQuery(id+"F9.wireOp",EDGE,"E49.4.4.0")}),1.0]])]});
            var Q51;
            Q51=makeQuery(id+"F9.imprint","IMPRINT",FACE,{"disambiguationData":[TD([[makeQuery(id+"F9.imprint","IMPRINT",EDGE,{"derivedFrom":sQuery(id+"F9.wireOp",EDGE,"E49.0.4.0")}),1.0]])]});
            var Q52;
            Q52=makeQuery(id+"F9.imprint","IMPRINT",FACE,{"disambiguationData":[TD([[makeQuery(id+"F9.imprint","IMPRINT",EDGE,{"derivedFrom":sQuery(id+"F9.wireOp",EDGE,"E49.1.4.0")}),1.0]])]});
            var Q53;
            Q53=makeQuery(id+"F9.imprint","IMPRINT",FACE,{"disambiguationData":[TD([[makeQuery(id+"F9.imprint","IMPRINT",EDGE,{"derivedFrom":sQuery(id+"F9.wireOp",EDGE,"E49.2.4.0")}),1.0]])]});
            var Q54;
            Q54=makeQuery(id+"F9.imprint","IMPRINT",FACE,{"disambiguationData":[TD([[makeQuery(id+"F9.imprint","IMPRINT",EDGE,{"derivedFrom":sQuery(id+"F9.wireOp",EDGE,"E49.3.4.0")}),1.0]])]});
            var Q55;
            Q55=makeQuery(id+"F9.imprint","IMPRINT",FACE,{"disambiguationData":[TD([[makeQuery(id+"F9.imprint","IMPRINT",EDGE,{"derivedFrom":sQuery(id+"F9.wireOp",EDGE,"E49.0.5.0")}),1.0]])]});
            var Q56;
            Q56=makeQuery(id+"F9.imprint","IMPRINT",FACE,{"disambiguationData":[TD([[makeQuery(id+"F9.imprint","IMPRINT",EDGE,{"derivedFrom":sQuery(id+"F9.wireOp",EDGE,"E49.1.5.0")}),1.0]])]});
            var Q57;
            Q57=makeQuery(id+"F9.imprint","IMPRINT",FACE,{"disambiguationData":[TD([[makeQuery(id+"F9.imprint","IMPRINT",EDGE,{"derivedFrom":sQuery(id+"F9.wireOp",EDGE,"E49.2.5.0")}),1.0]])]});
            var Q58;
            Q58=makeQuery(id+"F9.imprint","IMPRINT",FACE,{"disambiguationData":[TD([[makeQuery(id+"F9.imprint","IMPRINT",EDGE,{"derivedFrom":sQuery(id+"F9.wireOp",EDGE,"E49.3.5.0")}),1.0]])]});
            var Q59;
            Q59=makeQuery(id+"F9.imprint","IMPRINT",FACE,{"disambiguationData":[TD([[makeQuery(id+"F9.imprint","IMPRINT",EDGE,{"derivedFrom":sQuery(id+"F9.wireOp",EDGE,"E49.4.5.0")}),1.0]])]});
            var Q60;
            Q60=makeQuery(id+"F9.imprint","IMPRINT",FACE,{"disambiguationData":[TD([[makeQuery(id+"F9.imprint","IMPRINT",EDGE,{"derivedFrom":sQuery(id+"F9.wireOp",EDGE,"E49.5.5.0")}),1.0]])]});
            var Q61;
            Q61=makeQuery(id+"F9.imprint","IMPRINT",FACE,{"disambiguationData":[TD([[makeQuery(id+"F9.imprint","IMPRINT",EDGE,{"derivedFrom":sQuery(id+"F9.wireOp",EDGE,"E49.6.5.0")}),1.0]])]});
            var Q62;
            Q62=makeQuery(id+"F9.imprint","IMPRINT",FACE,{"disambiguationData":[TD([[makeQuery(id+"F9.imprint","IMPRINT",EDGE,{"derivedFrom":sQuery(id+"F9.wireOp",EDGE,"E49.7.5.0")}),1.0]])]});
            var Q63;
            Q63=makeQuery(id+"F9.imprint","IMPRINT",FACE,{"disambiguationData":[TD([[makeQuery(id+"F9.imprint","IMPRINT",EDGE,{"derivedFrom":sQuery(id+"F9.wireOp",EDGE,"E49.8.5.0")}),1.0]])]});
            var Q64;
            Q64=makeQuery(id+"F9.imprint","IMPRINT",FACE,{"disambiguationData":[TD([[makeQuery(id+"F9.imprint","IMPRINT",EDGE,{"derivedFrom":sQuery(id+"F9.wireOp",EDGE,"E49.9.5.0")}),1.0]])]});
            var Q65;
            Q65=makeQuery(id+"F9.imprint","IMPRINT",FACE,{"disambiguationData":[TD([[makeQuery(id+"F9.imprint","IMPRINT",EDGE,{"derivedFrom":sQuery(id+"F9.wireOp",EDGE,"E49.9.6.0")}),1.0]])]});
            var Q66;
            Q66=makeQuery(id+"F9.imprint","IMPRINT",FACE,{"disambiguationData":[TD([[makeQuery(id+"F9.imprint","IMPRINT",EDGE,{"derivedFrom":sQuery(id+"F9.wireOp",EDGE,"E49.8.6.0")}),1.0]])]});
            var Q67;
            Q67=makeQuery(id+"F9.imprint","IMPRINT",FACE,{"disambiguationData":[TD([[makeQuery(id+"F9.imprint","IMPRINT",EDGE,{"derivedFrom":sQuery(id+"F9.wireOp",EDGE,"E49.7.6.0")}),1.0]])]});
            var Q68;
            Q68=makeQuery(id+"F9.imprint","IMPRINT",FACE,{"disambiguationData":[TD([[makeQuery(id+"F9.imprint","IMPRINT",EDGE,{"derivedFrom":sQuery(id+"F9.wireOp",EDGE,"E49.6.6.0")}),1.0]])]});
            var Q69;
            Q69=makeQuery(id+"F9.imprint","IMPRINT",FACE,{"disambiguationData":[TD([[makeQuery(id+"F9.imprint","IMPRINT",EDGE,{"derivedFrom":sQuery(id+"F9.wireOp",EDGE,"E49.5.6.0")}),1.0]])]});
            var Q70;
            Q70=makeQuery(id+"F9.imprint","IMPRINT",FACE,{"disambiguationData":[TD([[makeQuery(id+"F9.imprint","IMPRINT",EDGE,{"derivedFrom":sQuery(id+"F9.wireOp",EDGE,"E49.4.6.0")}),1.0]])]});
            var Q71;
            Q71=makeQuery(id+"F9.imprint","IMPRINT",FACE,{"disambiguationData":[TD([[makeQuery(id+"F9.imprint","IMPRINT",EDGE,{"derivedFrom":sQuery(id+"F9.wireOp",EDGE,"E49.3.6.0")}),1.0]])]});
            var Q72;
            Q72=makeQuery(id+"F9.imprint","IMPRINT",FACE,{"disambiguationData":[TD([[makeQuery(id+"F9.imprint","IMPRINT",EDGE,{"derivedFrom":sQuery(id+"F9.wireOp",EDGE,"E49.2.6.0")}),1.0]])]});
            var Q73;
            Q73=makeQuery(id+"F9.imprint","IMPRINT",FACE,{"disambiguationData":[TD([[makeQuery(id+"F9.imprint","IMPRINT",EDGE,{"derivedFrom":sQuery(id+"F9.wireOp",EDGE,"E49.1.6.0")}),1.0]])]});
            var Q74;
            Q74=makeQuery(id+"F9.imprint","IMPRINT",FACE,{"disambiguationData":[TD([[makeQuery(id+"F9.imprint","IMPRINT",EDGE,{"derivedFrom":sQuery(id+"F9.wireOp",EDGE,"E49.0.6.0")}),1.0]])]});
            extrude(context, id + "F10", {"entities" : qUnion([Q0, Q1, Q2, Q3, Q4, Q5, Q6, Q7, Q8, Q9, Q10, Q11, Q12, Q13, Q14, Q15, Q16, Q17, Q18, Q19, Q20, Q21, Q22, Q23, Q24, Q25, Q26, Q27, Q28, Q29, Q30, Q31, Q32, Q33, Q34, Q35, Q36, Q37, Q38, Q39, Q40, Q41, Q42, Q43, Q44, Q45, Q46, Q47, Q48, Q49, Q50, Q51, Q52, Q53, Q54, Q55, Q56, Q57, Q58, Q59, Q60, Q61, Q62, Q63, Q64, Q65, Q66, Q67, Q68, Q69, Q70, Q71, Q72, Q73, Q74]), "operationType" : NewBodyOperationType.REMOVE, "oppositeDirection" : true, "depth" : 25.4 * mm});
        }
        {
            var Q0;
            Q0=makeQuery(id+"F0.imprint","IMPRINT",FACE,{"disambiguationData":[TD([[makeQuery(id+"F0.imprint","IMPRINT",EDGE,{"derivedFrom":sQuery(id+"F0.wireOp",EDGE,"E0.bottom")}),-1.0]])]});
            var sketch = newSketch(context, id + "F11", { "sketchPlane" : qUnion([Q0])});
            skLineSegment(sketch, "E50", {"start": v(0, 0) * mm, "end": v(0, 177.8) * mm});
            skLineSegment(sketch, "E51", {"start": v(0, 0) * mm, "end": v(0, -177.8) * mm});
            skLineSegment(sketch, "E52", {"start": v(0, 88.9) * mm, "end": v(-12.7, 88.9) * mm});
            skLineSegment(sketch, "E53", {"start": v(0, -177.8) * mm, "end": v(-12.7, -177.8) * mm});
            skLineSegment(sketch, "E54", {"start": v(-12.7, -177.8) * mm, "end": v(-12.7, 177.8) * mm});
            skLineSegment(sketch, "E55", {"start": v(-12.7, 177.8) * mm, "end": v(-12.7, 165.1) * mm});
            skLineSegment(sketch, "E56", {"start": v(-12.7, 165.1) * mm, "end": v(-241.3, 165.1) * mm});
            skLineSegment(sketch, "E57", {"start": v(-241.3, 165.1) * mm, "end": v(-241.3, -165.1) * mm});
            skLineSegment(sketch, "E58", {"start": v(-241.3, -165.1) * mm, "end": v(-12.7, -165.1) * mm});
            skLineSegment(sketch, "E59.MirrorCS", {"start": v(12.7, 165.1) * mm, "end": v(241.3, 165.1) * mm});
            skLineSegment(sketch, "E60.MirrorCS", {"start": v(241.3, 165.1) * mm, "end": v(241.3, -165.1) * mm});
            skLineSegment(sketch, "E61.MirrorCS", {"start": v(241.3, -165.1) * mm, "end": v(12.7, -165.1) * mm});
            skLineSegment(sketch, "E62", {"start": v(12.7, 165.1) * mm, "end": v(12.7, -165.1) * mm});
            skLineSegment(sketch, "E63", {"start": v(-241.3, -165.1) * mm, "end": v(-190.5, -165.1) * mm});
            skLineSegment(sketch, "E64", {"start": v(-190.5, -165.1) * mm, "end": v(-190.5, -114.3) * mm});
            skLineSegment(sketch, "E65", {"start": v(-190.5, -114.3) * mm, "end": v(-63.5, -114.3) * mm});
            skLineSegment(sketch, "E66", {"start": v(-63.5, -114.3) * mm, "end": v(-63.5, 114.3) * mm});
            skLineSegment(sketch, "E67", {"start": v(-63.5, 114.3) * mm, "end": v(-190.5, 114.3) * mm});
            skCircle(sketch, "E68", {"center": v(-190.5, 114.3) * mm, "radius": 6.35 * mm});
            skCircle(sketch, "E69", {"center": v(-63.5, 114.3) * mm, "radius": 6.35 * mm});
            skCircle(sketch, "E70", {"center": v(-63.5, -114.3) * mm, "radius": 6.35 * mm});
            skCircle(sketch, "E71", {"center": v(-190.5, -114.3) * mm, "radius": 6.35 * mm});
            skCircle(sketch, "E72.MirrorC", {"center": v(63.5, 114.3) * mm, "radius": 6.35 * mm});
            skCircle(sketch, "E73.MirrorC", {"center": v(190.5, 114.3) * mm, "radius": 6.35 * mm});
            skCircle(sketch, "E74.MirrorC", {"center": v(190.5, -114.3) * mm, "radius": 6.35 * mm});
            skCircle(sketch, "E75.MirrorC", {"center": v(63.5, -114.3) * mm, "radius": 6.35 * mm});
            skSolve(sketch);
        }
        {
            var Q0;
            {var subQ10=sQuery(id+"F11.wireOp",EDGE,"E56");Q0=makeQuery(id+"F11.imprint","IMPRINT",FACE,{"disambiguationData":[TD([[makeQuery(id+"F11.imprint","IMPRINT",EDGE,{"derivedFrom":subQ10}),1.0]])]});}
            var Q1;
            Q1=makeQuery(id+"F11.imprint","IMPRINT",FACE,{"disambiguationData":[TD([[makeQuery(id+"F11.imprint","IMPRINT",EDGE,{"derivedFrom":sQuery(id+"F11.wireOp",EDGE,"E59.MirrorCS")}),-1.0]])]});
            var Q2;
            Q2=makeQuery(id+"F11.imprint","IMPRINT",FACE,{"disambiguationData":[TD([[makeQuery(id+"F11.imprint","IMPRINT",EDGE,{"derivedFrom":sQuery(id+"F11.wireOp",EDGE,"E68")}),1.0]])]});
            var Q3;
            {var subQ0=sQuery(id+"F11.wireOp",EDGE,"E66");var subQ1=sQuery(id+"F11.wireOp",EDGE,"E65");var subQ2=makeQuery(id+"F11.imprint","INTERSECT",VERTEX,{"derivedFrom":[subQ1,subQ0]});Q3=makeQuery(id+"F11.imprint","IMPRINT",FACE,{"disambiguationData":[TD([[makeQuery(id+"F11.imprint","IMPRINT",EDGE,{"disambiguationData":[TD([[subQ2,1.0]])],"derivedFrom":subQ1}),1.0]])]});}
            var Q4;
            {var subQ0=sQuery(id+"F11.wireOp",EDGE,"E66");var subQ1=sQuery(id+"F11.wireOp",EDGE,"E65");var subQ2=makeQuery(id+"F11.imprint","INTERSECT",VERTEX,{"derivedFrom":[subQ1,subQ0]});Q4=makeQuery(id+"F11.imprint","IMPRINT",FACE,{"disambiguationData":[TD([[makeQuery(id+"F11.imprint","IMPRINT",EDGE,{"disambiguationData":[TD([[subQ2,1.0]])],"derivedFrom":subQ1}),-1.0]])]});}
            var Q5;
            {var subQ0=sQuery(id+"F11.wireOp",EDGE,"E67");var subQ1=sQuery(id+"F11.wireOp",EDGE,"E66");var subQ2=makeQuery(id+"F11.imprint","INTERSECT",VERTEX,{"derivedFrom":[subQ1,subQ0]});Q5=makeQuery(id+"F11.imprint","IMPRINT",FACE,{"disambiguationData":[TD([[makeQuery(id+"F11.imprint","IMPRINT",EDGE,{"disambiguationData":[TD([[subQ2,1.0]])],"derivedFrom":subQ1}),1.0]])]});}
            var Q6;
            {var subQ0=sQuery(id+"F11.wireOp",EDGE,"E67");var subQ1=sQuery(id+"F11.wireOp",EDGE,"E66");var subQ2=makeQuery(id+"F11.imprint","INTERSECT",VERTEX,{"derivedFrom":[subQ1,subQ0]});Q6=makeQuery(id+"F11.imprint","IMPRINT",FACE,{"disambiguationData":[TD([[makeQuery(id+"F11.imprint","IMPRINT",EDGE,{"disambiguationData":[TD([[subQ2,1.0]])],"derivedFrom":subQ1}),-1.0]])]});}
            var Q7;
            {var subQ0=sQuery(id+"F11.wireOp",EDGE,"E65");var subQ1=sQuery(id+"F11.wireOp",EDGE,"E64");var subQ2=makeQuery(id+"F11.imprint","INTERSECT",VERTEX,{"derivedFrom":[subQ1,subQ0]});Q7=makeQuery(id+"F11.imprint","IMPRINT",FACE,{"disambiguationData":[TD([[makeQuery(id+"F11.imprint","IMPRINT",EDGE,{"disambiguationData":[TD([[subQ2,1.0]])],"derivedFrom":subQ1}),-1.0]])]});}
            var Q8;
            {var subQ0=sQuery(id+"F11.wireOp",EDGE,"E65");var subQ1=sQuery(id+"F11.wireOp",EDGE,"E64");var subQ2=makeQuery(id+"F11.imprint","INTERSECT",VERTEX,{"derivedFrom":[subQ1,subQ0]});Q8=makeQuery(id+"F11.imprint","IMPRINT",FACE,{"disambiguationData":[TD([[makeQuery(id+"F11.imprint","IMPRINT",EDGE,{"disambiguationData":[TD([[subQ2,1.0]])],"derivedFrom":subQ1}),1.0]])]});}
            var Q9;
            Q9=makeQuery(id+"F11.imprint","IMPRINT",FACE,{"disambiguationData":[TD([[makeQuery(id+"F11.imprint","IMPRINT",EDGE,{"derivedFrom":sQuery(id+"F11.wireOp",EDGE,"E75.MirrorC")}),-1.0]])]});
            var Q10;
            Q10=makeQuery(id+"F11.imprint","IMPRINT",FACE,{"disambiguationData":[TD([[makeQuery(id+"F11.imprint","IMPRINT",EDGE,{"derivedFrom":sQuery(id+"F11.wireOp",EDGE,"E74.MirrorC")}),-1.0]])]});
            var Q11;
            Q11=makeQuery(id+"F11.imprint","IMPRINT",FACE,{"disambiguationData":[TD([[makeQuery(id+"F11.imprint","IMPRINT",EDGE,{"derivedFrom":sQuery(id+"F11.wireOp",EDGE,"E72.MirrorC")}),-1.0]])]});
            var Q12;
            Q12=makeQuery(id+"F11.imprint","IMPRINT",FACE,{"disambiguationData":[TD([[makeQuery(id+"F11.imprint","IMPRINT",EDGE,{"derivedFrom":sQuery(id+"F11.wireOp",EDGE,"E73.MirrorC")}),-1.0]])]});
            extrude(context, id + "F12", {"entities" : qUnion([Q0, Q1, Q2, Q3, Q4, Q5, Q6, Q7, Q8, Q9, Q10, Q11, Q12]), "depth" : 25.4 * mm});
        }
        {
            var Q0;
            Q0=makeQuery(id+"F11.imprint","IMPRINT",FACE,{"disambiguationData":[TD([[makeQuery(id+"F11.imprint","IMPRINT",EDGE,{"derivedFrom":sQuery(id+"F11.wireOp",EDGE,"E68")}),1.0]])]});
            var Q1;
            {var subQ0=sQuery(id+"F11.wireOp",EDGE,"E67");var subQ1=sQuery(id+"F11.wireOp",EDGE,"E66");var subQ2=makeQuery(id+"F11.imprint","INTERSECT",VERTEX,{"derivedFrom":[subQ1,subQ0]});Q1=makeQuery(id+"F11.imprint","IMPRINT",FACE,{"disambiguationData":[TD([[makeQuery(id+"F11.imprint","IMPRINT",EDGE,{"disambiguationData":[TD([[subQ2,1.0]])],"derivedFrom":subQ1}),-1.0]])]});}
            var Q2;
            {var subQ0=sQuery(id+"F11.wireOp",EDGE,"E66");var subQ1=sQuery(id+"F11.wireOp",EDGE,"E65");var subQ2=makeQuery(id+"F11.imprint","INTERSECT",VERTEX,{"derivedFrom":[subQ1,subQ0]});Q2=makeQuery(id+"F11.imprint","IMPRINT",FACE,{"disambiguationData":[TD([[makeQuery(id+"F11.imprint","IMPRINT",EDGE,{"disambiguationData":[TD([[subQ2,1.0]])],"derivedFrom":subQ1}),-1.0]])]});}
            var Q3;
            {var subQ0=sQuery(id+"F11.wireOp",EDGE,"E66");var subQ1=sQuery(id+"F11.wireOp",EDGE,"E65");var subQ2=makeQuery(id+"F11.imprint","INTERSECT",VERTEX,{"derivedFrom":[subQ1,subQ0]});Q3=makeQuery(id+"F11.imprint","IMPRINT",FACE,{"disambiguationData":[TD([[makeQuery(id+"F11.imprint","IMPRINT",EDGE,{"disambiguationData":[TD([[subQ2,1.0]])],"derivedFrom":subQ1}),1.0]])]});}
            var Q4;
            {var subQ0=sQuery(id+"F11.wireOp",EDGE,"E65");var subQ1=sQuery(id+"F11.wireOp",EDGE,"E64");var subQ2=makeQuery(id+"F11.imprint","INTERSECT",VERTEX,{"derivedFrom":[subQ1,subQ0]});Q4=makeQuery(id+"F11.imprint","IMPRINT",FACE,{"disambiguationData":[TD([[makeQuery(id+"F11.imprint","IMPRINT",EDGE,{"disambiguationData":[TD([[subQ2,1.0]])],"derivedFrom":subQ1}),1.0]])]});}
            var Q5;
            {var subQ0=sQuery(id+"F11.wireOp",EDGE,"E65");var subQ1=sQuery(id+"F11.wireOp",EDGE,"E64");var subQ2=makeQuery(id+"F11.imprint","INTERSECT",VERTEX,{"derivedFrom":[subQ1,subQ0]});Q5=makeQuery(id+"F11.imprint","IMPRINT",FACE,{"disambiguationData":[TD([[makeQuery(id+"F11.imprint","IMPRINT",EDGE,{"disambiguationData":[TD([[subQ2,1.0]])],"derivedFrom":subQ1}),-1.0]])]});}
            var Q6;
            Q6=makeQuery(id+"F11.imprint","IMPRINT",FACE,{"disambiguationData":[TD([[makeQuery(id+"F11.imprint","IMPRINT",EDGE,{"derivedFrom":sQuery(id+"F11.wireOp",EDGE,"E75.MirrorC")}),-1.0]])]});
            var Q7;
            Q7=makeQuery(id+"F11.imprint","IMPRINT",FACE,{"disambiguationData":[TD([[makeQuery(id+"F11.imprint","IMPRINT",EDGE,{"derivedFrom":sQuery(id+"F11.wireOp",EDGE,"E74.MirrorC")}),-1.0]])]});
            var Q8;
            Q8=makeQuery(id+"F11.imprint","IMPRINT",FACE,{"disambiguationData":[TD([[makeQuery(id+"F11.imprint","IMPRINT",EDGE,{"derivedFrom":sQuery(id+"F11.wireOp",EDGE,"E73.MirrorC")}),-1.0]])]});
            var Q9;
            Q9=makeQuery(id+"F11.imprint","IMPRINT",FACE,{"disambiguationData":[TD([[makeQuery(id+"F11.imprint","IMPRINT",EDGE,{"derivedFrom":sQuery(id+"F11.wireOp",EDGE,"E72.MirrorC")}),-1.0]])]});
            var Q10;
            {var subQ0=sQuery(id+"F11.wireOp",EDGE,"E67");var subQ1=sQuery(id+"F11.wireOp",EDGE,"E66");var subQ2=makeQuery(id+"F11.imprint","INTERSECT",VERTEX,{"derivedFrom":[subQ1,subQ0]});Q10=makeQuery(id+"F11.imprint","IMPRINT",FACE,{"disambiguationData":[TD([[makeQuery(id+"F11.imprint","IMPRINT",EDGE,{"disambiguationData":[TD([[subQ2,1.0]])],"derivedFrom":subQ1}),1.0]])]});}
            extrude(context, id + "F13", {"entities" : qUnion([Q0, Q1, Q2, Q3, Q4, Q5, Q6, Q7, Q8, Q9, Q10]), "operationType" : NewBodyOperationType.REMOVE, "oppositeDirection" : true, "depth" : 25.4 * mm});
        }
        {
            var Q0;
            Q0=makeQuery(id+"F11.imprint","IMPRINT",FACE,{"disambiguationData":[TD([[makeQuery(id+"F11.imprint","IMPRINT",EDGE,{"derivedFrom":sQuery(id+"F11.wireOp",EDGE,"E72.MirrorC")}),-1.0]])]});
            var Q1;
            Q1=makeQuery(id+"F11.imprint","IMPRINT",FACE,{"disambiguationData":[TD([[makeQuery(id+"F11.imprint","IMPRINT",EDGE,{"derivedFrom":sQuery(id+"F11.wireOp",EDGE,"E74.MirrorC")}),-1.0]])]});
            var Q2;
            Q2=makeQuery(id+"F11.imprint","IMPRINT",FACE,{"disambiguationData":[TD([[makeQuery(id+"F11.imprint","IMPRINT",EDGE,{"derivedFrom":sQuery(id+"F11.wireOp",EDGE,"E75.MirrorC")}),-1.0]])]});
            var Q3;
            Q3=makeQuery(id+"F11.imprint","IMPRINT",FACE,{"disambiguationData":[TD([[makeQuery(id+"F11.imprint","IMPRINT",EDGE,{"derivedFrom":sQuery(id+"F11.wireOp",EDGE,"E73.MirrorC")}),-1.0]])]});
            var Q4;
            {var subQ0=sQuery(id+"F11.wireOp",EDGE,"E66");var subQ1=sQuery(id+"F11.wireOp",EDGE,"E65");var subQ2=makeQuery(id+"F11.imprint","INTERSECT",VERTEX,{"derivedFrom":[subQ1,subQ0]});Q4=makeQuery(id+"F11.imprint","IMPRINT",FACE,{"disambiguationData":[TD([[makeQuery(id+"F11.imprint","IMPRINT",EDGE,{"disambiguationData":[TD([[subQ2,1.0]])],"derivedFrom":subQ1}),-1.0]])]});}
            var Q5;
            {var subQ0=sQuery(id+"F11.wireOp",EDGE,"E66");var subQ1=sQuery(id+"F11.wireOp",EDGE,"E65");var subQ2=makeQuery(id+"F11.imprint","INTERSECT",VERTEX,{"derivedFrom":[subQ1,subQ0]});Q5=makeQuery(id+"F11.imprint","IMPRINT",FACE,{"disambiguationData":[TD([[makeQuery(id+"F11.imprint","IMPRINT",EDGE,{"disambiguationData":[TD([[subQ2,1.0]])],"derivedFrom":subQ1}),1.0]])]});}
            var Q6;
            {var subQ0=sQuery(id+"F11.wireOp",EDGE,"E65");var subQ1=sQuery(id+"F11.wireOp",EDGE,"E64");var subQ2=makeQuery(id+"F11.imprint","INTERSECT",VERTEX,{"derivedFrom":[subQ1,subQ0]});Q6=makeQuery(id+"F11.imprint","IMPRINT",FACE,{"disambiguationData":[TD([[makeQuery(id+"F11.imprint","IMPRINT",EDGE,{"disambiguationData":[TD([[subQ2,1.0]])],"derivedFrom":subQ1}),1.0]])]});}
            var Q7;
            {var subQ0=sQuery(id+"F11.wireOp",EDGE,"E65");var subQ1=sQuery(id+"F11.wireOp",EDGE,"E64");var subQ2=makeQuery(id+"F11.imprint","INTERSECT",VERTEX,{"derivedFrom":[subQ1,subQ0]});Q7=makeQuery(id+"F11.imprint","IMPRINT",FACE,{"disambiguationData":[TD([[makeQuery(id+"F11.imprint","IMPRINT",EDGE,{"disambiguationData":[TD([[subQ2,1.0]])],"derivedFrom":subQ1}),-1.0]])]});}
            var Q8;
            {var subQ0=sQuery(id+"F11.wireOp",EDGE,"E67");var subQ1=sQuery(id+"F11.wireOp",EDGE,"E66");var subQ2=makeQuery(id+"F11.imprint","INTERSECT",VERTEX,{"derivedFrom":[subQ1,subQ0]});Q8=makeQuery(id+"F11.imprint","IMPRINT",FACE,{"disambiguationData":[TD([[makeQuery(id+"F11.imprint","IMPRINT",EDGE,{"disambiguationData":[TD([[subQ2,1.0]])],"derivedFrom":subQ1}),-1.0]])]});}
            var Q9;
            {var subQ0=sQuery(id+"F11.wireOp",EDGE,"E67");var subQ1=sQuery(id+"F11.wireOp",EDGE,"E66");var subQ2=makeQuery(id+"F11.imprint","INTERSECT",VERTEX,{"derivedFrom":[subQ1,subQ0]});Q9=makeQuery(id+"F11.imprint","IMPRINT",FACE,{"disambiguationData":[TD([[makeQuery(id+"F11.imprint","IMPRINT",EDGE,{"disambiguationData":[TD([[subQ2,1.0]])],"derivedFrom":subQ1}),1.0]])]});}
            var Q10;
            Q10=makeQuery(id+"F11.imprint","IMPRINT",FACE,{"disambiguationData":[TD([[makeQuery(id+"F11.imprint","IMPRINT",EDGE,{"derivedFrom":sQuery(id+"F11.wireOp",EDGE,"E68")}),1.0]])]});
            var Q11;
            Q11=sQuery(id+"F11.wireOp",EDGE,"E68");
            var Q12;
            Q12=sQuery(id+"F11.wireOp",EDGE,"E69");
            var Q13;
            Q13=sQuery(id+"F11.wireOp",EDGE,"E72.MirrorC");
            var Q14;
            Q14=sQuery(id+"F11.wireOp",EDGE,"E73.MirrorC");
            var Q15;
            Q15=sQuery(id+"F11.wireOp",EDGE,"E74.MirrorC");
            var Q16;
            Q16=sQuery(id+"F11.wireOp",EDGE,"E75.MirrorC");
            var Q17;
            Q17=sQuery(id+"F11.wireOp",EDGE,"E70");
            var Q18;
            Q18=sQuery(id+"F11.wireOp",EDGE,"E71");
            extrude(context, id + "F14", {"entities" : qUnion([Q0, Q1, Q2, Q3, Q4, Q5, Q6, Q7, Q8, Q9, Q10]), "operationType" : NewBodyOperationType.REMOVE, "surfaceEntities" : qUnion([Q11, Q12, Q13, Q14, Q15, Q16, Q17, Q18]), "depth" : 12.7 * mm});
        }
        {
            var Q0;
            Q0=makeQuery(id+"F12.opExtrude","CAP_FACE",FACE,{"disambiguationData":[OSD([sQuery(id+"F11.wireOp",EDGE,"E54"),sQuery(id+"F11.wireOp",EDGE,"E56"),sQuery(id+"F11.wireOp",EDGE,"E57"),sQuery(id+"F11.wireOp",EDGE,"E58"),sQuery(id+"F11.wireOp",EDGE,"E63")])],"isStart":false});
            var sketch = newSketch(context, id + "F15", { "sketchPlane" : qUnion([Q0])});
            skCircle(sketch, "E76", {"center": v(-127, -152.4) * mm, "radius": 3.33 * mm});
            skCircle(sketch, "E77.0.1.0", {"center": v(-127, -127) * mm, "radius": 3.33 * mm});
            skCircle(sketch, "E77.0.2.0", {"center": v(-127, -101.6) * mm, "radius": 3.33 * mm});
            skCircle(sketch, "E77.0.3.0", {"center": v(-127, -76.2) * mm, "radius": 3.33 * mm});
            skCircle(sketch, "E77.0.4.0", {"center": v(-127, -50.8) * mm, "radius": 3.33 * mm});
            skCircle(sketch, "E77.0.5.0", {"center": v(-127, -25.4) * mm, "radius": 3.33 * mm});
            skCircle(sketch, "E77.0.6.0", {"center": v(-127, 0) * mm, "radius": 3.33 * mm});
            skCircle(sketch, "E77.0.7.0", {"center": v(-127, 25.4) * mm, "radius": 3.33 * mm});
            skCircle(sketch, "E77.0.8.0", {"center": v(-127, 50.8) * mm, "radius": 3.33 * mm});
            skCircle(sketch, "E77.0.9.0", {"center": v(-127, 76.2) * mm, "radius": 3.33 * mm});
            skCircle(sketch, "E77.0.10.0", {"center": v(-127, 101.6) * mm, "radius": 3.33 * mm});
            skCircle(sketch, "E77.0.11.0", {"center": v(-127, 127) * mm, "radius": 3.33 * mm});
            skCircle(sketch, "E77.0.12.0", {"center": v(-127, 152.4) * mm, "radius": 3.33 * mm});
            skLineSegment(sketch, "E77.direction1", {"start": v(-127, -152.4) * mm, "end": v(-101.6, -152.4) * mm, "construction": true});
            skLineSegment(sketch, "E77.direction2", {"start": v(-127, -152.4) * mm, "end": v(-127, -127) * mm, "construction": true});
            skSolve(sketch);
        }
        {
            var Q0;
            Q0 = qSketchRegion(id + "F15", true);
            extrude(context, id + "F16", {"entities" : qUnion([Q0]), "operationType" : NewBodyOperationType.REMOVE, "oppositeDirection" : true, "depth" : 11.43 * mm});
        }
        {
            var Q0;
            Q0=makeQuery(id+"F12.opExtrude","CAP_FACE",FACE,{"disambiguationData":[OSD([sQuery(id+"F11.wireOp",EDGE,"E54"),sQuery(id+"F11.wireOp",EDGE,"E56"),sQuery(id+"F11.wireOp",EDGE,"E57"),sQuery(id+"F11.wireOp",EDGE,"E58"),sQuery(id+"F11.wireOp",EDGE,"E63")])],"isStart":false});
            var sketch = newSketch(context, id + "F17", { "sketchPlane" : qUnion([Q0])});
            skLineSegment(sketch, "E78.bottom", {"start": v(-85.73, -165.1) * mm, "end": v(-168.28, -165.1) * mm});
            skLineSegment(sketch, "E78.top", {"start": v(-85.73, -139.7) * mm, "end": v(-168.28, -139.7) * mm});
            skLineSegment(sketch, "E78.left", {"start": v(-85.73, -165.1) * mm, "end": v(-85.73, -139.7) * mm});
            skLineSegment(sketch, "E78.right", {"start": v(-168.28, -165.1) * mm, "end": v(-168.28, -139.7) * mm});
            skPoint(sketch, "E78.middle", {"position": v(-127, -152.4) * mm});
            skLineSegment(sketch, "E79", {"start": v(-168.28, -152.4) * mm, "end": v(-174.63, -152.4) * mm});
            skLineSegment(sketch, "E80", {"start": v(-85.73, -152.4) * mm, "end": v(-79.38, -152.4) * mm});
            skLineSegment(sketch, "E81.bottom", {"start": v(-174.63, -165.1) * mm, "end": v(-241.3, -165.1) * mm});
            skLineSegment(sketch, "E81.top", {"start": v(-174.63, 165.1) * mm, "end": v(-241.3, 165.1) * mm});
            skLineSegment(sketch, "E81.left", {"start": v(-174.63, -165.1) * mm, "end": v(-174.63, 165.1) * mm});
            skLineSegment(sketch, "E81.right", {"start": v(-241.3, -165.1) * mm, "end": v(-241.3, 165.1) * mm});
            skLineSegment(sketch, "E82.bottom", {"start": v(-79.38, -165.1) * mm, "end": v(-12.7, -165.1) * mm});
            skLineSegment(sketch, "E82.top", {"start": v(-79.38, 165.1) * mm, "end": v(-12.7, 165.1) * mm});
            skLineSegment(sketch, "E82.left", {"start": v(-79.38, -165.1) * mm, "end": v(-79.38, 165.1) * mm});
            skLineSegment(sketch, "E82.right", {"start": v(-12.7, -165.1) * mm, "end": v(-12.7, 165.1) * mm});
            skSolve(sketch);
        }
        {
            var Q0;
            {var subQ3=sQuery(id+"F17.wireOp",EDGE,"E81.bottom");Q0=makeQuery(id+"F17.imprint","IMPRINT",FACE,{"disambiguationData":[TD([[makeQuery(id+"F17.imprint","IMPRINT",EDGE,{"derivedFrom":subQ3}),1.0]])]});}
            var Q1;
            {var subQ3=sQuery(id+"F17.wireOp",EDGE,"E82.bottom");Q1=makeQuery(id+"F17.imprint","IMPRINT",FACE,{"disambiguationData":[TD([[makeQuery(id+"F17.imprint","IMPRINT",EDGE,{"derivedFrom":subQ3}),1.0]])]});}
            extrude(context, id + "F18", {"entities" : qUnion([Q0, Q1]), "depth" : 14.73 * mm});
        }
        {
            var Q0;
            Q0=makeQuery(id+"F18.opExtrude","CAP_FACE",FACE,{"disambiguationData":[OSD([sQuery(id+"F17.wireOp",EDGE,"E81.bottom"),sQuery(id+"F17.wireOp",EDGE,"E81.top"),sQuery(id+"F17.wireOp",EDGE,"E81.left"),sQuery(id+"F17.wireOp",EDGE,"E81.right")])],"isStart":false});
            var sketch = newSketch(context, id + "F19", { "sketchPlane" : qUnion([Q0])});
            skLineSegment(sketch, "E83", {"start": v(-207.96, -165.1) * mm, "end": v(-207.96, -139.7) * mm});
            skCircle(sketch, "E84", {"center": v(-207.96, -139.7) * mm, "radius": 4.83 * mm});
            skCircle(sketch, "E85.0.1.0", {"center": v(-207.96, -69.85) * mm, "radius": 4.83 * mm});
            skCircle(sketch, "E85.0.2.0", {"center": v(-207.96, 0) * mm, "radius": 4.83 * mm});
            skCircle(sketch, "E85.0.3.0", {"center": v(-207.96, 69.85) * mm, "radius": 4.83 * mm});
            skCircle(sketch, "E85.0.4.0", {"center": v(-207.96, 139.7) * mm, "radius": 4.83 * mm});
            skLineSegment(sketch, "E85.direction1", {"start": v(-207.96, -139.7) * mm, "end": v(-182.56, -139.7) * mm, "construction": true});
            skLineSegment(sketch, "E85.direction2", {"start": v(-207.96, -139.7) * mm, "end": v(-207.96, -69.85) * mm, "construction": true});
            skSolve(sketch);
        }
        {
            var Q0;
            Q0 = qSketchRegion(id + "F19", true);
            extrude(context, id + "F20", {"entities" : qUnion([Q0]), "operationType" : NewBodyOperationType.REMOVE, "oppositeDirection" : true, "depth" : 25.4 * mm});
        }
        {
            var Q0;
            Q0=makeQuery(id+"F12.opExtrude","CAP_FACE",FACE,{"disambiguationData":[OSD([sQuery(id+"F11.wireOp",EDGE,"E54"),sQuery(id+"F11.wireOp",EDGE,"E56"),sQuery(id+"F11.wireOp",EDGE,"E57"),sQuery(id+"F11.wireOp",EDGE,"E58"),sQuery(id+"F11.wireOp",EDGE,"E63")])],"isStart":false});
            var sketch = newSketch(context, id + "F21", { "sketchPlane" : qUnion([Q0])});
            skLineSegment(sketch, "E86", {"start": v(-241.3, -165.1) * mm, "end": v(-207.96, -165.1) * mm});
            skLineSegment(sketch, "E87", {"start": v(-207.96, -165.1) * mm, "end": v(-207.96, -139.7) * mm});
            skCircle(sketch, "E88", {"center": v(-207.96, -139.7) * mm, "radius": 4.04 * mm});
            skLineSegment(sketch, "E89", {"start": v(-207.96, -139.7) * mm, "end": v(-46.04, -139.7) * mm});
            skCircle(sketch, "E90.0.1.0", {"center": v(-207.96, -69.85) * mm, "radius": 4.04 * mm});
            skCircle(sketch, "E90.0.2.0", {"center": v(-207.96, 0) * mm, "radius": 4.04 * mm});
            skCircle(sketch, "E90.0.3.0", {"center": v(-207.96, 69.85) * mm, "radius": 4.04 * mm});
            skCircle(sketch, "E90.0.4.0", {"center": v(-207.96, 139.7) * mm, "radius": 4.04 * mm});
            skCircle(sketch, "E90.1.0.0", {"center": v(-46.04, -139.7) * mm, "radius": 4.04 * mm});
            skCircle(sketch, "E90.1.1.0", {"center": v(-46.04, -69.85) * mm, "radius": 4.04 * mm});
            skCircle(sketch, "E90.1.2.0", {"center": v(-46.04, 0) * mm, "radius": 4.04 * mm});
            skCircle(sketch, "E90.1.3.0", {"center": v(-46.04, 69.85) * mm, "radius": 4.04 * mm});
            skCircle(sketch, "E90.1.4.0", {"center": v(-46.04, 139.7) * mm, "radius": 4.04 * mm});
            skLineSegment(sketch, "E90.direction1", {"start": v(-207.96, -139.7) * mm, "end": v(-46.04, -139.7) * mm, "construction": true});
            skLineSegment(sketch, "E90.direction2", {"start": v(-207.96, -139.7) * mm, "end": v(-207.96, -69.85) * mm, "construction": true});
            skSolve(sketch);
        }
        {
            var Q0;
            Q0 = qSketchRegion(id + "F21", true);
            extrude(context, id + "F22", {"entities" : qUnion([Q0]), "operationType" : NewBodyOperationType.REMOVE, "oppositeDirection" : true, "depth" : 12.7 * mm});
        }
        {
            var Q0;
            Q0=makeQuery(id+"F18.opExtrude","CAP_FACE",FACE,{"disambiguationData":[OSD([sQuery(id+"F17.wireOp",EDGE,"E82.bottom"),sQuery(id+"F17.wireOp",EDGE,"E82.top"),sQuery(id+"F17.wireOp",EDGE,"E82.left"),sQuery(id+"F17.wireOp",EDGE,"E82.right")])],"isStart":false});
            var sketch = newSketch(context, id + "F23", { "sketchPlane" : qUnion([Q0])});
            skLineSegment(sketch, "E91", {"start": v(-46.04, -165.1) * mm, "end": v(-46.04, -139.7) * mm});
            skCircle(sketch, "E92", {"center": v(-46.04, -139.7) * mm, "radius": 4.83 * mm});
            skCircle(sketch, "E93.0.1.0", {"center": v(-46.04, -69.85) * mm, "radius": 4.83 * mm});
            skCircle(sketch, "E93.0.2.0", {"center": v(-46.04, 0) * mm, "radius": 4.83 * mm});
            skCircle(sketch, "E93.0.3.0", {"center": v(-46.04, 69.85) * mm, "radius": 4.83 * mm});
            skCircle(sketch, "E93.0.4.0", {"center": v(-46.04, 139.7) * mm, "radius": 4.83 * mm});
            skLineSegment(sketch, "E93.direction1", {"start": v(-46.04, -139.7) * mm, "end": v(-20.64, -139.7) * mm, "construction": true});
            skLineSegment(sketch, "E93.direction2", {"start": v(-46.04, -139.7) * mm, "end": v(-46.04, -69.85) * mm, "construction": true});
            skSolve(sketch);
        }
        {
            var Q0;
            Q0 = qSketchRegion(id + "F23", true);
            extrude(context, id + "F24", {"entities" : qUnion([Q0]), "operationType" : NewBodyOperationType.REMOVE, "oppositeDirection" : true, "depth" : 25.4 * mm});
        }
        {
            var Q0;
            Q0=makeQuery(id+"F18.opExtrude","CAP_FACE",FACE,{"disambiguationData":[OSD([sQuery(id+"F17.wireOp",EDGE,"E82.bottom"),sQuery(id+"F17.wireOp",EDGE,"E82.top"),sQuery(id+"F17.wireOp",EDGE,"E82.left"),sQuery(id+"F17.wireOp",EDGE,"E82.right")])],"isStart":false});
            var sketch = newSketch(context, id + "F25", { "sketchPlane" : qUnion([Q0])});
            skCircle(sketch, "E94", {"center": v(-46.04, 139.7) * mm, "radius": 7.62 * mm});
            skCircle(sketch, "E95", {"center": v(-46.04, 69.85) * mm, "radius": 7.62 * mm});
            skCircle(sketch, "E96", {"center": v(-46.04, 0) * mm, "radius": 7.62 * mm});
            skCircle(sketch, "E97", {"center": v(-46.04, -69.85) * mm, "radius": 7.62 * mm});
            skCircle(sketch, "E98", {"center": v(-46.04, -139.7) * mm, "radius": 7.62 * mm});
            skLineSegment(sketch, "E99", {"start": v(-46.04, -139.7) * mm, "end": v(-207.96, -139.7) * mm});
            skCircle(sketch, "E100", {"center": v(-207.96, -139.7) * mm, "radius": 7.62 * mm});
            skCircle(sketch, "E101.0.1.0", {"center": v(-207.96, -69.85) * mm, "radius": 7.62 * mm});
            skCircle(sketch, "E101.0.2.0", {"center": v(-207.96, 0) * mm, "radius": 7.62 * mm});
            skCircle(sketch, "E101.0.3.0", {"center": v(-207.96, 69.85) * mm, "radius": 7.62 * mm});
            skCircle(sketch, "E101.0.4.0", {"center": v(-207.96, 139.7) * mm, "radius": 7.62 * mm});
            skLineSegment(sketch, "E101.direction1", {"start": v(-207.96, -139.7) * mm, "end": v(-182.56, -139.7) * mm, "construction": true});
            skLineSegment(sketch, "E101.direction2", {"start": v(-207.96, -139.7) * mm, "end": v(-207.96, -69.85) * mm, "construction": true});
            skSolve(sketch);
        }
        {
            var Q0;
            Q0=makeQuery(id+"F9.imprint","IMPRINT",FACE,{"disambiguationData":[TD([[makeQuery(id+"F9.imprint","IMPRINT",EDGE,{"derivedFrom":sQuery(id+"F9.wireOp",EDGE,"E49.4.6.0")}),1.0]])]});
            var Q1;
            Q1=makeQuery(id+"F9.imprint","IMPRINT",FACE,{"disambiguationData":[TD([[makeQuery(id+"F9.imprint","IMPRINT",EDGE,{"derivedFrom":sQuery(id+"F9.wireOp",EDGE,"E49.4.0.0")}),1.0]])]});
            var Q2;
            Q2=makeQuery(id+"F9.imprint","IMPRINT",FACE,{"disambiguationData":[TD([[makeQuery(id+"F9.imprint","IMPRINT",EDGE,{"derivedFrom":sQuery(id+"F9.wireOp",EDGE,"E49.0.6.0")}),1.0]])]});
            var Q3;
            Q3=makeQuery(id+"F9.imprint","IMPRINT",FACE,{"disambiguationData":[TD([[makeQuery(id+"F9.imprint","IMPRINT",EDGE,{"derivedFrom":sQuery(id+"F9.wireOp",EDGE,"E48")}),1.0]])]});
            extrude(context, id + "F26", {"entities" : qUnion([Q0, Q1, Q2, Q3]), "operationType" : NewBodyOperationType.REMOVE, "depth" : 76.2 * mm});
        }
        {
            var Q0;
            Q0 = qSketchRegion(id + "F25", true);
            extrude(context, id + "F27", {"entities" : qUnion([Q0]), "operationType" : NewBodyOperationType.REMOVE, "oppositeDirection" : true, "depth" : 9.65 * mm});
        }
        {
            var Q0;
            Q0=makeQuery(id+"F12.opExtrude","CAP_FACE",FACE,{"disambiguationData":[OSD([sQuery(id+"F11.wireOp",EDGE,"E59.MirrorCS"),sQuery(id+"F11.wireOp",EDGE,"E60.MirrorCS"),sQuery(id+"F11.wireOp",EDGE,"E61.MirrorCS"),sQuery(id+"F11.wireOp",EDGE,"E62")])],"isStart":false});
            var sketch = newSketch(context, id + "F28", { "sketchPlane" : qUnion([Q0])});
            skPoint(sketch, "E102.endSnap0", {"position": v(12.7, 120.95) * mm});
            skPoint(sketch, "E103.endSnap0", {"position": v(12.7, -120.95) * mm});
            skLineSegment(sketch, "E104", {"start": v(127, 165.1) * mm, "end": v(127, 63.5) * mm});
            skLineSegment(sketch, "E105", {"start": v(12.7, 114.3) * mm, "end": v(12.7, 99.36) * mm});
            skLineSegment(sketch, "E106", {"start": v(12.7, 99.36) * mm, "end": v(241.3, 99.36) * mm});
            skLineSegment(sketch, "E107", {"start": v(241.3, 99.36) * mm, "end": v(241.3, 129.24) * mm});
            skLineSegment(sketch, "E108", {"start": v(241.3, 129.24) * mm, "end": v(12.7, 129.24) * mm});
            skLineSegment(sketch, "E109", {"start": v(12.7, 129.24) * mm, "end": v(12.7, 114.3) * mm});
            skLineSegment(sketch, "E110", {"start": v(127, 0) * mm, "end": v(152.4, 0) * mm});
            skPoint(sketch, "E110.startSnap0", {"position": v(127, -165.1) * mm});
            skLineSegment(sketch, "E111.MirrorCS", {"start": v(12.7, -99.36) * mm, "end": v(241.3, -99.36) * mm});
            skLineSegment(sketch, "E112.MirrorCS", {"start": v(241.3, -129.24) * mm, "end": v(12.7, -129.24) * mm});
            skLineSegment(sketch, "E113.MirrorCS", {"start": v(241.3, -99.36) * mm, "end": v(241.3, -129.24) * mm});
            skLineSegment(sketch, "E114.MirrorCS", {"start": v(12.7, -114.3) * mm, "end": v(12.7, -99.36) * mm});
            skLineSegment(sketch, "E115.MirrorCS", {"start": v(12.7, -129.24) * mm, "end": v(12.7, -114.3) * mm});
            skCircle(sketch, "E116", {"center": v(127, 114.3) * mm, "radius": 3.33 * mm});
            skLineSegment(sketch, "E117", {"start": v(127, -129.24) * mm, "end": v(126.6, -99.36) * mm});
            skCircle(sketch, "E118", {"center": v(126.8, -114.3) * mm, "radius": 3.33 * mm});
            skLineSegment(sketch, "E119.bottom", {"start": v(12.7, 165.1) * mm, "end": v(74.1, 165.1) * mm});
            skLineSegment(sketch, "E119.top", {"start": v(12.7, 63.5) * mm, "end": v(74.1, 63.5) * mm});
            skLineSegment(sketch, "E119.left", {"start": v(12.7, 165.1) * mm, "end": v(12.7, 63.5) * mm});
            skLineSegment(sketch, "E119.right", {"start": v(74.1, 165.1) * mm, "end": v(74.1, 63.5) * mm});
            skLineSegment(sketch, "E120.MirrorCS", {"start": v(179.9, 165.1) * mm, "end": v(179.9, 63.5) * mm});
            skLineSegment(sketch, "E121.MirrorCS", {"start": v(241.3, 63.5) * mm, "end": v(179.9, 63.5) * mm});
            skLineSegment(sketch, "E122.MirrorCS", {"start": v(241.3, 165.1) * mm, "end": v(241.3, 63.5) * mm});
            skLineSegment(sketch, "E123.MirrorCS", {"start": v(241.3, 165.1) * mm, "end": v(179.9, 165.1) * mm});
            skLineSegment(sketch, "E124.MirrorCS", {"start": v(241.3, -63.5) * mm, "end": v(179.9, -63.5) * mm});
            skLineSegment(sketch, "E125.MirrorCS", {"start": v(179.9, -165.1) * mm, "end": v(179.9, -63.5) * mm});
            skLineSegment(sketch, "E126.MirrorCS", {"start": v(241.3, -165.1) * mm, "end": v(241.3, -63.5) * mm});
            skLineSegment(sketch, "E127.MirrorCS", {"start": v(74.1, -165.1) * mm, "end": v(74.1, -63.5) * mm});
            skLineSegment(sketch, "E128.MirrorCS", {"start": v(12.7, -63.5) * mm, "end": v(74.1, -63.5) * mm});
            skLineSegment(sketch, "E129.MirrorCS", {"start": v(12.7, -165.1) * mm, "end": v(12.7, -63.5) * mm});
            skLineSegment(sketch, "E130.MirrorCS", {"start": v(12.7, -165.1) * mm, "end": v(74.1, -165.1) * mm});
            skLineSegment(sketch, "E131.MirrorCS", {"start": v(241.3, -165.1) * mm, "end": v(179.9, -165.1) * mm});
            skPoint(sketch, "E132.endSnap0", {"position": v(43.4, 139.7) * mm});
            skCircle(sketch, "E133", {"center": v(43.4, 139.7) * mm, "radius": 4.83 * mm});
            skCircle(sketch, "E134", {"center": v(210.6, 139.7) * mm, "radius": 4.83 * mm});
            skCircle(sketch, "E135", {"center": v(43.4, -88.9) * mm, "radius": 4.83 * mm});
            skCircle(sketch, "E136", {"center": v(43.4, -139.7) * mm, "radius": 4.83 * mm});
            skCircle(sketch, "E137", {"center": v(210.6, -139.7) * mm, "radius": 4.83 * mm});
            skCircle(sketch, "E138", {"center": v(210.6, -88.9) * mm, "radius": 4.83 * mm});
            skCircle(sketch, "E139", {"center": v(210.6, 88.9) * mm, "radius": 4.83 * mm});
            skCircle(sketch, "E140", {"center": v(43.4, 88.9) * mm, "radius": 4.83 * mm});
            skCircle(sketch, "E141", {"center": v(43.4, 139.7) * mm, "radius": 3.33 * mm});
            skCircle(sketch, "E142", {"center": v(210.6, 139.7) * mm, "radius": 3.33 * mm});
            skCircle(sketch, "E143", {"center": v(210.6, 88.9) * mm, "radius": 3.33 * mm});
            skCircle(sketch, "E144", {"center": v(43.4, 88.9) * mm, "radius": 3.33 * mm});
            skCircle(sketch, "E145", {"center": v(43.4, -88.9) * mm, "radius": 3.33 * mm});
            skCircle(sketch, "E146", {"center": v(43.4, -139.7) * mm, "radius": 3.33 * mm});
            skCircle(sketch, "E147", {"center": v(210.6, -139.7) * mm, "radius": 3.33 * mm});
            skCircle(sketch, "E148", {"center": v(210.6, -88.9) * mm, "radius": 3.33 * mm});
            skSolve(sketch);
        }
        {
            var Q0;
            {var subQ0=sQuery(id+"F28.wireOp",EDGE,"E119.left");var subQ1=sQuery(id+"F28.wireOp",EDGE,"XHsj2Bdy-5fj5-9Be5-5Zvq-8SLI1EAt6y1m");var subQ2=makeQuery(id+"F28.imprint","INTERSECT",VERTEX,{"derivedFrom":[subQ1,subQ0]});Q0=makeQuery(id+"F28.imprint","IMPRINT",FACE,{"disambiguationData":[TD([[makeQuery(id+"F28.imprint","IMPRINT",EDGE,{"disambiguationData":[TD([[subQ2,1.0]])],"derivedFrom":subQ1}),1.0]])]});}
            var Q1;
            {var subQ0=sQuery(id+"F28.wireOp",EDGE,"E119.left");var subQ1=sQuery(id+"F28.wireOp",EDGE,"XHsj2Bdy-5fj5-9Be5-5Zvq-8SLI1EAt6y1m");var subQ2=makeQuery(id+"F28.imprint","INTERSECT",VERTEX,{"derivedFrom":[subQ1,subQ0]});Q1=makeQuery(id+"F28.imprint","IMPRINT",FACE,{"disambiguationData":[TD([[makeQuery(id+"F28.imprint","IMPRINT",EDGE,{"disambiguationData":[TD([[subQ2,1.0]])],"derivedFrom":subQ1}),-1.0]])]});}
            var Q2;
            {var subQ0=sQuery(id+"F28.wireOp",EDGE,"E122.MirrorCS");var subQ1=sQuery(id+"F28.wireOp",EDGE,"E106");var subQ2=makeQuery(id+"F28.imprint","INTERSECT",VERTEX,{"derivedFrom":[subQ1,subQ0]});Q2=makeQuery(id+"F28.imprint","IMPRINT",FACE,{"disambiguationData":[TD([[makeQuery(id+"F28.imprint","IMPRINT",EDGE,{"disambiguationData":[TD([[subQ2,1.0]])],"derivedFrom":subQ1}),1.0]])]});}
            var Q3;
            {var subQ0=sQuery(id+"F28.wireOp",EDGE,"E129.MirrorCS");var subQ1=sQuery(id+"F28.wireOp",EDGE,"E111.MirrorCS");var subQ2=makeQuery(id+"F28.imprint","INTERSECT",VERTEX,{"derivedFrom":[subQ1,subQ0]});Q3=makeQuery(id+"F28.imprint","IMPRINT",FACE,{"disambiguationData":[TD([[makeQuery(id+"F28.imprint","IMPRINT",EDGE,{"disambiguationData":[TD([[subQ2,-1.0]])],"derivedFrom":subQ1}),-1.0]])]});}
            var Q4;
            {var subQ0=sQuery(id+"F28.wireOp",EDGE,"E126.MirrorCS");var subQ1=sQuery(id+"F28.wireOp",EDGE,"E111.MirrorCS");var subQ2=makeQuery(id+"F28.imprint","INTERSECT",VERTEX,{"derivedFrom":[subQ1,subQ0]});Q4=makeQuery(id+"F28.imprint","IMPRINT",FACE,{"disambiguationData":[TD([[makeQuery(id+"F28.imprint","IMPRINT",EDGE,{"disambiguationData":[TD([[subQ2,1.0]])],"derivedFrom":subQ1}),-1.0]])]});}
            var Q5;
            {var subQ1=sQuery(id+"F28.wireOp",EDGE,"E104");var subQ5=sQuery(id+"F28.wireOp",EDGE,"E108");var subQ6=makeQuery(id+"F28.imprint","INTERSECT",VERTEX,{"derivedFrom":[subQ1,subQ5]});Q5=makeQuery(id+"F28.imprint","IMPRINT",FACE,{"disambiguationData":[TD([[makeQuery(id+"F28.imprint","IMPRINT",EDGE,{"disambiguationData":[TD([[subQ6,-1.0]])],"derivedFrom":subQ1}),-1.0]])]});}
            var Q6;
            {var subQ1=sQuery(id+"F28.wireOp",EDGE,"E104");var subQ5=sQuery(id+"F28.wireOp",EDGE,"E106");var subQ6=makeQuery(id+"F28.imprint","INTERSECT",VERTEX,{"derivedFrom":[subQ1,subQ5]});Q6=makeQuery(id+"F28.imprint","IMPRINT",FACE,{"disambiguationData":[TD([[makeQuery(id+"F28.imprint","IMPRINT",EDGE,{"disambiguationData":[TD([[subQ6,1.0]])],"derivedFrom":subQ1}),-1.0]])]});}
            var Q7;
            {var subQ0=sQuery(id+"F28.wireOp",EDGE,"E117");var subQ1=sQuery(id+"F28.wireOp",EDGE,"E111.MirrorCS");var subQ2=makeQuery(id+"F28.imprint","INTERSECT",VERTEX,{"derivedFrom":[subQ1,subQ0]});Q7=makeQuery(id+"F28.imprint","IMPRINT",FACE,{"disambiguationData":[TD([[makeQuery(id+"F28.imprint","IMPRINT",EDGE,{"disambiguationData":[TD([[subQ2,1.0]])],"derivedFrom":subQ1}),-1.0]])]});}
            var Q8;
            {var subQ0=sQuery(id+"F28.wireOp",EDGE,"E117");var subQ1=sQuery(id+"F28.wireOp",EDGE,"E111.MirrorCS");var subQ2=makeQuery(id+"F28.imprint","INTERSECT",VERTEX,{"derivedFrom":[subQ1,subQ0]});Q8=makeQuery(id+"F28.imprint","IMPRINT",FACE,{"disambiguationData":[TD([[makeQuery(id+"F28.imprint","IMPRINT",EDGE,{"disambiguationData":[TD([[subQ2,-1.0]])],"derivedFrom":subQ1}),-1.0]])]});}
            var Q9;
            {var subQ0=sQuery(id+"F28.wireOp",EDGE,"E108");var subQ1=sQuery(id+"F28.wireOp",EDGE,"E104");var subQ2=makeQuery(id+"F28.imprint","INTERSECT",VERTEX,{"derivedFrom":[subQ1,subQ0]});Q9=makeQuery(id+"F28.imprint","IMPRINT",FACE,{"disambiguationData":[TD([[makeQuery(id+"F28.imprint","IMPRINT",EDGE,{"disambiguationData":[TD([[subQ2,-1.0]])],"derivedFrom":subQ1}),1.0]])]});}
            var Q10;
            {var subQ0=sQuery(id+"F28.wireOp",EDGE,"E104");var subQ1=makeQuery(id+"F28.imprint","INTERSECT",VERTEX,{"derivedFrom":[subQ0,sQuery(id+"F28.wireOp",EDGE,"XHsj2Bdy-5fj5-9Be5-5Zvq-8SLI1EAt6y1m")]});Q10=makeQuery(id+"F28.imprint","IMPRINT",FACE,{"disambiguationData":[TD([[makeQuery(id+"F28.imprint","IMPRINT",EDGE,{"disambiguationData":[TD([[subQ1,1.0]])],"derivedFrom":subQ0}),1.0]])]});}
            var Q11;
            {var subQ0=sQuery(id+"F28.wireOp",EDGE,"XHsj2Bdy-5fj5-9Be5-5Zvq-8SLI1EAt6y1m");var subQ1=sQuery(id+"F28.wireOp",EDGE,"E104");var subQ2=makeQuery(id+"F28.imprint","INTERSECT",VERTEX,{"derivedFrom":[subQ1,subQ0]});Q11=makeQuery(id+"F28.imprint","IMPRINT",FACE,{"disambiguationData":[TD([[makeQuery(id+"F28.imprint","IMPRINT",EDGE,{"disambiguationData":[TD([[subQ2,-1.0]])],"derivedFrom":subQ1}),-1.0]])]});}
            var Q12;
            {var subQ0=sQuery(id+"F28.wireOp",EDGE,"XHsj2Bdy-5fj5-9Be5-5Zvq-8SLI1EAt6y1m");var subQ1=sQuery(id+"F28.wireOp",EDGE,"E104");var subQ2=makeQuery(id+"F28.imprint","INTERSECT",VERTEX,{"derivedFrom":[subQ1,subQ0]});Q12=makeQuery(id+"F28.imprint","IMPRINT",FACE,{"disambiguationData":[TD([[makeQuery(id+"F28.imprint","IMPRINT",EDGE,{"disambiguationData":[TD([[subQ2,1.0]])],"derivedFrom":subQ1}),-1.0]])]});}
            var Q13;
            {var subQ0=sQuery(id+"F28.wireOp",EDGE,"E118");var subQ1=sQuery(id+"F28.wireOp",EDGE,"E117");var subQ2=makeQuery(id+"F28.imprint","INTERSECT",VERTEX,{"disambiguationData":[OD(0.0)],"derivedFrom":[subQ1,subQ0]});Q13=makeQuery(id+"F28.imprint","IMPRINT",FACE,{"disambiguationData":[TD([[makeQuery(id+"F28.imprint","IMPRINT",EDGE,{"disambiguationData":[TD([[subQ2,-1.0]])],"derivedFrom":subQ1}),-1.0]])]});}
            var Q14;
            {var subQ0=sQuery(id+"F28.wireOp",EDGE,"E118");var subQ1=sQuery(id+"F28.wireOp",EDGE,"E117");var subQ2=makeQuery(id+"F28.imprint","INTERSECT",VERTEX,{"disambiguationData":[OD(0.0)],"derivedFrom":[subQ1,subQ0]});Q14=makeQuery(id+"F28.imprint","IMPRINT",FACE,{"disambiguationData":[TD([[makeQuery(id+"F28.imprint","IMPRINT",EDGE,{"disambiguationData":[TD([[subQ2,-1.0]])],"derivedFrom":subQ1}),1.0]])]});}
            var Q15;
            {var subQ0=sQuery(id+"F28.wireOp",EDGE,"E41HQL2S-HR8c-D0n9-kxV9-eGqN4JmXdrcO");var subQ5=sQuery(id+"F28.wireOp",EDGE,"E108");var subQ6=makeQuery(id+"F28.imprint","INTERSECT",VERTEX,{"derivedFrom":[subQ5,subQ0]});Q15=makeQuery(id+"F28.imprint","IMPRINT",FACE,{"disambiguationData":[TD([[makeQuery(id+"F28.imprint","IMPRINT",EDGE,{"disambiguationData":[TD([[subQ6,-1.0]])],"derivedFrom":subQ5}),1.0]])]});}
            var Q16;
            {var subQ3=sQuery(id+"F28.wireOp",EDGE,"E132");var subQ5=sQuery(id+"F28.wireOp",EDGE,"E106");var subQ6=makeQuery(id+"F28.imprint","INTERSECT",VERTEX,{"derivedFrom":[subQ5,subQ3]});Q16=makeQuery(id+"F28.imprint","IMPRINT",FACE,{"disambiguationData":[TD([[makeQuery(id+"F28.imprint","IMPRINT",EDGE,{"disambiguationData":[TD([[subQ6,-1.0]])],"derivedFrom":subQ5}),1.0]])]});}
            var Q17;
            {var subQ0=sQuery(id+"F28.wireOp",EDGE,"9WtMLiPp-tRfW-MAJF-Tqf3-JbQfPx4JElf0");var subQ5=sQuery(id+"F28.wireOp",EDGE,"E106");var subQ6=makeQuery(id+"F28.imprint","INTERSECT",VERTEX,{"derivedFrom":[subQ5,subQ0]});Q17=makeQuery(id+"F28.imprint","IMPRINT",FACE,{"disambiguationData":[TD([[makeQuery(id+"F28.imprint","IMPRINT",EDGE,{"disambiguationData":[TD([[subQ6,-1.0]])],"derivedFrom":subQ5}),1.0]])]});}
            var Q18;
            {var subQ3=sQuery(id+"F28.wireOp",EDGE,"E119.right");var subQ5=sQuery(id+"F28.wireOp",EDGE,"E108");var subQ6=makeQuery(id+"F28.imprint","INTERSECT",VERTEX,{"derivedFrom":[subQ5,subQ3]});Q18=makeQuery(id+"F28.imprint","IMPRINT",FACE,{"disambiguationData":[TD([[makeQuery(id+"F28.imprint","IMPRINT",EDGE,{"disambiguationData":[TD([[subQ6,-1.0]])],"derivedFrom":subQ5}),1.0]])]});}
            var Q19;
            {var subQ0=sQuery(id+"F28.wireOp",EDGE,"E120.MirrorCS");var subQ1=sQuery(id+"F28.wireOp",EDGE,"E106");var subQ2=makeQuery(id+"F28.imprint","INTERSECT",VERTEX,{"derivedFrom":[subQ1,subQ0]});Q19=makeQuery(id+"F28.imprint","IMPRINT",FACE,{"disambiguationData":[TD([[makeQuery(id+"F28.imprint","IMPRINT",EDGE,{"disambiguationData":[TD([[subQ2,-1.0]])],"derivedFrom":subQ1}),1.0]])]});}
            var Q20;
            {var subQ0=sQuery(id+"F28.wireOp",EDGE,"zD1DPgNz-dfj1-2HkU-o1YG-glmSUdlLRjYE");var subQ3=sQuery(id+"F28.wireOp",EDGE,"E106");var subQ4=makeQuery(id+"F28.imprint","INTERSECT",VERTEX,{"derivedFrom":[subQ3,subQ0]});Q20=makeQuery(id+"F28.imprint","IMPRINT",FACE,{"disambiguationData":[TD([[makeQuery(id+"F28.imprint","IMPRINT",EDGE,{"disambiguationData":[TD([[subQ4,-1.0]])],"derivedFrom":subQ3}),1.0]])]});}
            var Q21;
            {var subQ0=sQuery(id+"F28.wireOp",EDGE,"E125.MirrorCS");var subQ1=sQuery(id+"F28.wireOp",EDGE,"E111.MirrorCS");var subQ2=makeQuery(id+"F28.imprint","INTERSECT",VERTEX,{"derivedFrom":[subQ1,subQ0]});Q21=makeQuery(id+"F28.imprint","IMPRINT",FACE,{"disambiguationData":[TD([[makeQuery(id+"F28.imprint","IMPRINT",EDGE,{"disambiguationData":[TD([[subQ2,-1.0]])],"derivedFrom":subQ1}),-1.0]])]});}
            var Q22;
            {var subQ0=sQuery(id+"F28.wireOp",EDGE,"Cobala6K-nph9-bkYj-TdKu-PGzEkCbEPjE5");var subQ3=sQuery(id+"F28.wireOp",EDGE,"E111.MirrorCS");var subQ4=makeQuery(id+"F28.imprint","INTERSECT",VERTEX,{"derivedFrom":[subQ3,subQ0]});Q22=makeQuery(id+"F28.imprint","IMPRINT",FACE,{"disambiguationData":[TD([[makeQuery(id+"F28.imprint","IMPRINT",EDGE,{"disambiguationData":[TD([[subQ4,-1.0]])],"derivedFrom":subQ3}),-1.0]])]});}
            var Q23;
            {var subQ1=sQuery(id+"F28.wireOp",EDGE,"IlPbpYRA-JeQV-qnHW-QBER-wy8PiDBLE379");var subQ3=sQuery(id+"F28.wireOp",EDGE,"E111.MirrorCS");var subQ4=makeQuery(id+"F28.imprint","INTERSECT",VERTEX,{"derivedFrom":[subQ3,subQ1]});Q23=makeQuery(id+"F28.imprint","IMPRINT",FACE,{"disambiguationData":[TD([[makeQuery(id+"F28.imprint","IMPRINT",EDGE,{"disambiguationData":[TD([[subQ4,-1.0]])],"derivedFrom":subQ3}),-1.0]])]});}
            extrude(context, id + "F29", {"entities" : qUnion([Q0, Q1, Q2, Q3, Q4, Q5, Q6, Q7, Q8, Q9, Q10, Q11, Q12, Q13, Q14, Q15, Q16, Q17, Q18, Q19, Q20, Q21, Q22, Q23]), "operationType" : NewBodyOperationType.REMOVE, "oppositeDirection" : true, "depth" : 1.78 * mm});
        }
        {
            var Q0;
            Q0=makeQuery(id+"F18.opExtrude","CAP_FACE",FACE,{"disambiguationData":[OSD([sQuery(id+"F17.wireOp",EDGE,"E81.bottom"),sQuery(id+"F17.wireOp",EDGE,"E81.top"),sQuery(id+"F17.wireOp",EDGE,"E81.left"),sQuery(id+"F17.wireOp",EDGE,"E81.right")])],"isStart":false});
            var sketch = newSketch(context, id + "F30", { "sketchPlane" : qUnion([Q0])});
            skCircle(sketch, "E149", {"center": v(-228.6, 152.4) * mm, "radius": 7.62 * mm});
            skCircle(sketch, "E150", {"center": v(-228.6, -152.4) * mm, "radius": 7.62 * mm});
            skLineSegment(sketch, "E151", {"start": v(-228.6, 152.4) * mm, "end": v(-25.4, 152.4) * mm});
            skLineSegment(sketch, "E152", {"start": v(-25.4, 152.4) * mm, "end": v(-25.4, -152.4) * mm});
            skCircle(sketch, "E153", {"center": v(-25.4, 152.4) * mm, "radius": 7.62 * mm});
            skCircle(sketch, "E154", {"center": v(-25.4, -152.4) * mm, "radius": 7.62 * mm});
            skSolve(sketch);
        }
        {
            var Q0;
            {var subQ0=sQuery(id+"F28.wireOp",EDGE,"E118");var subQ1=sQuery(id+"F28.wireOp",EDGE,"E117");var subQ2=makeQuery(id+"F28.imprint","INTERSECT",VERTEX,{"disambiguationData":[OD(0.0)],"derivedFrom":[subQ1,subQ0]});Q0=makeQuery(id+"F28.imprint","IMPRINT",FACE,{"disambiguationData":[TD([[makeQuery(id+"F28.imprint","IMPRINT",EDGE,{"disambiguationData":[TD([[subQ2,-1.0]])],"derivedFrom":subQ1}),-1.0]])]});}
            var Q1;
            {var subQ0=sQuery(id+"F28.wireOp",EDGE,"E118");var subQ1=sQuery(id+"F28.wireOp",EDGE,"E117");var subQ2=makeQuery(id+"F28.imprint","INTERSECT",VERTEX,{"disambiguationData":[OD(0.0)],"derivedFrom":[subQ1,subQ0]});Q1=makeQuery(id+"F28.imprint","IMPRINT",FACE,{"disambiguationData":[TD([[makeQuery(id+"F28.imprint","IMPRINT",EDGE,{"disambiguationData":[TD([[subQ2,-1.0]])],"derivedFrom":subQ1}),1.0]])]});}
            var Q2;
            {var subQ0=sQuery(id+"F28.wireOp",EDGE,"E116");var subQ1=sQuery(id+"F28.wireOp",EDGE,"E104");var subQ2=makeQuery(id+"F28.imprint","INTERSECT",VERTEX,{"disambiguationData":[OD(0.0)],"derivedFrom":[subQ1,subQ0]});Q2=makeQuery(id+"F28.imprint","IMPRINT",FACE,{"disambiguationData":[TD([[makeQuery(id+"F28.imprint","IMPRINT",EDGE,{"disambiguationData":[TD([[subQ2,-1.0]])],"derivedFrom":subQ1}),-1.0]])]});}
            var Q3;
            {var subQ0=sQuery(id+"F28.wireOp",EDGE,"E116");var subQ1=sQuery(id+"F28.wireOp",EDGE,"E104");var subQ2=makeQuery(id+"F28.imprint","INTERSECT",VERTEX,{"disambiguationData":[OD(0.0)],"derivedFrom":[subQ1,subQ0]});Q3=makeQuery(id+"F28.imprint","IMPRINT",FACE,{"disambiguationData":[TD([[makeQuery(id+"F28.imprint","IMPRINT",EDGE,{"disambiguationData":[TD([[subQ2,-1.0]])],"derivedFrom":subQ1}),1.0]])]});}
            extrude(context, id + "F31", {"entities" : qUnion([Q0, Q1, Q2, Q3]), "operationType" : NewBodyOperationType.REMOVE, "oppositeDirection" : true, "depth" : 17.78 * mm});
        }
        {
            var Q0;
            Q0 = qSketchRegion(id + "F30", true);
            extrude(context, id + "F32", {"entities" : qUnion([Q0]), "operationType" : NewBodyOperationType.REMOVE, "oppositeDirection" : true, "depth" : 10.16 * mm});
        }
        {
            var Q0;
            {var subQ1=sQuery(id+"F28.wireOp",EDGE,"E119.top");Q0=makeQuery(id+"F28.imprint","IMPRINT",FACE,{"disambiguationData":[TD([[makeQuery(id+"F28.imprint","IMPRINT",EDGE,{"derivedFrom":subQ1}),1.0]])]});}
            var Q1;
            {var subQ1=sQuery(id+"F28.wireOp",EDGE,"E119.bottom");Q1=makeQuery(id+"F28.imprint","IMPRINT",FACE,{"disambiguationData":[TD([[makeQuery(id+"F28.imprint","IMPRINT",EDGE,{"derivedFrom":subQ1}),-1.0]])]});}
            var Q2;
            {var subQ0=sQuery(id+"F28.wireOp",EDGE,"E123.MirrorCS");Q2=makeQuery(id+"F28.imprint","IMPRINT",FACE,{"disambiguationData":[TD([[makeQuery(id+"F28.imprint","IMPRINT",EDGE,{"derivedFrom":subQ0}),-1.0]])]});}
            var Q3;
            {var subQ0=sQuery(id+"F28.wireOp",EDGE,"E122.MirrorCS");var subQ1=sQuery(id+"F28.wireOp",EDGE,"E106");var subQ2=makeQuery(id+"F28.imprint","INTERSECT",VERTEX,{"derivedFrom":[subQ1,subQ0]});Q3=makeQuery(id+"F28.imprint","IMPRINT",FACE,{"disambiguationData":[TD([[makeQuery(id+"F28.imprint","IMPRINT",EDGE,{"disambiguationData":[TD([[subQ2,1.0]])],"derivedFrom":subQ1}),1.0]])]});}
            var Q4;
            {var subQ0=sQuery(id+"F28.wireOp",EDGE,"E121.MirrorCS");Q4=makeQuery(id+"F28.imprint","IMPRINT",FACE,{"disambiguationData":[TD([[makeQuery(id+"F28.imprint","IMPRINT",EDGE,{"derivedFrom":subQ0}),-1.0]])]});}
            var Q5;
            {var subQ3=sQuery(id+"F28.wireOp",EDGE,"E124.MirrorCS");Q5=makeQuery(id+"F28.imprint","IMPRINT",FACE,{"disambiguationData":[TD([[makeQuery(id+"F28.imprint","IMPRINT",EDGE,{"derivedFrom":subQ3}),1.0]])]});}
            var Q6;
            {var subQ0=sQuery(id+"F28.wireOp",EDGE,"E126.MirrorCS");var subQ1=sQuery(id+"F28.wireOp",EDGE,"E111.MirrorCS");var subQ2=makeQuery(id+"F28.imprint","INTERSECT",VERTEX,{"derivedFrom":[subQ1,subQ0]});Q6=makeQuery(id+"F28.imprint","IMPRINT",FACE,{"disambiguationData":[TD([[makeQuery(id+"F28.imprint","IMPRINT",EDGE,{"disambiguationData":[TD([[subQ2,1.0]])],"derivedFrom":subQ1}),-1.0]])]});}
            var Q7;
            {var subQ0=sQuery(id+"F28.wireOp",EDGE,"E131.MirrorCS");Q7=makeQuery(id+"F28.imprint","IMPRINT",FACE,{"disambiguationData":[TD([[makeQuery(id+"F28.imprint","IMPRINT",EDGE,{"derivedFrom":subQ0}),-1.0]])]});}
            var Q8;
            {var subQ0=sQuery(id+"F28.wireOp",EDGE,"E130.MirrorCS");Q8=makeQuery(id+"F28.imprint","IMPRINT",FACE,{"disambiguationData":[TD([[makeQuery(id+"F28.imprint","IMPRINT",EDGE,{"derivedFrom":subQ0}),-1.0]])]});}
            var Q9;
            {var subQ0=sQuery(id+"F28.wireOp",EDGE,"E129.MirrorCS");var subQ1=sQuery(id+"F28.wireOp",EDGE,"E111.MirrorCS");var subQ2=makeQuery(id+"F28.imprint","INTERSECT",VERTEX,{"derivedFrom":[subQ1,subQ0]});Q9=makeQuery(id+"F28.imprint","IMPRINT",FACE,{"disambiguationData":[TD([[makeQuery(id+"F28.imprint","IMPRINT",EDGE,{"disambiguationData":[TD([[subQ2,-1.0]])],"derivedFrom":subQ1}),-1.0]])]});}
            var Q10;
            {var subQ3=sQuery(id+"F28.wireOp",EDGE,"E128.MirrorCS");Q10=makeQuery(id+"F28.imprint","IMPRINT",FACE,{"disambiguationData":[TD([[makeQuery(id+"F28.imprint","IMPRINT",EDGE,{"derivedFrom":subQ3}),-1.0]])]});}
            var Q11;
            {var subQ0=sQuery(id+"F28.wireOp",EDGE,"E126.MirrorCS");var subQ1=sQuery(id+"F28.wireOp",EDGE,"E111.MirrorCS");var subQ2=makeQuery(id+"F28.imprint","INTERSECT",VERTEX,{"derivedFrom":[subQ1,subQ0]});Q11=makeQuery(id+"F28.imprint","IMPRINT",FACE,{"disambiguationData":[TD([[makeQuery(id+"F28.imprint","IMPRINT",EDGE,{"disambiguationData":[TD([[subQ2,1.0]])],"derivedFrom":subQ1}),-1.0]])]});}
            var Q12;
            {var subQ0=sQuery(id+"F28.wireOp",EDGE,"E129.MirrorCS");var subQ1=sQuery(id+"F28.wireOp",EDGE,"E111.MirrorCS");var subQ2=makeQuery(id+"F28.imprint","INTERSECT",VERTEX,{"derivedFrom":[subQ1,subQ0]});Q12=makeQuery(id+"F28.imprint","IMPRINT",FACE,{"disambiguationData":[TD([[makeQuery(id+"F28.imprint","IMPRINT",EDGE,{"disambiguationData":[TD([[subQ2,-1.0]])],"derivedFrom":subQ1}),-1.0]])]});}
            var Q13;
            {var subQ0=sQuery(id+"F28.wireOp",EDGE,"E126.MirrorCS");var subQ1=sQuery(id+"F28.wireOp",EDGE,"E111.MirrorCS");var subQ2=makeQuery(id+"F28.imprint","INTERSECT",VERTEX,{"derivedFrom":[subQ1,subQ0]});Q13=makeQuery(id+"F28.imprint","IMPRINT",FACE,{"disambiguationData":[TD([[makeQuery(id+"F28.imprint","IMPRINT",EDGE,{"disambiguationData":[TD([[subQ2,1.0]])],"derivedFrom":subQ1}),-1.0]])]});}
            var Q14;
            {var subQ3=sQuery(id+"F28.wireOp",EDGE,"E124.MirrorCS");Q14=makeQuery(id+"F28.imprint","IMPRINT",FACE,{"disambiguationData":[TD([[makeQuery(id+"F28.imprint","IMPRINT",EDGE,{"derivedFrom":subQ3}),1.0]])]});}
            var Q15;
            {var subQ0=sQuery(id+"F28.wireOp",EDGE,"E129.MirrorCS");var subQ1=sQuery(id+"F28.wireOp",EDGE,"E111.MirrorCS");var subQ2=makeQuery(id+"F28.imprint","INTERSECT",VERTEX,{"derivedFrom":[subQ1,subQ0]});Q15=makeQuery(id+"F28.imprint","IMPRINT",FACE,{"disambiguationData":[TD([[makeQuery(id+"F28.imprint","IMPRINT",EDGE,{"disambiguationData":[TD([[subQ2,-1.0]])],"derivedFrom":subQ1}),-1.0]])]});}
            var Q16;
            {var subQ0=sQuery(id+"F28.wireOp",EDGE,"E126.MirrorCS");var subQ1=sQuery(id+"F28.wireOp",EDGE,"E111.MirrorCS");var subQ2=makeQuery(id+"F28.imprint","INTERSECT",VERTEX,{"derivedFrom":[subQ1,subQ0]});Q16=makeQuery(id+"F28.imprint","IMPRINT",FACE,{"disambiguationData":[TD([[makeQuery(id+"F28.imprint","IMPRINT",EDGE,{"disambiguationData":[TD([[subQ2,1.0]])],"derivedFrom":subQ1}),-1.0]])]});}
            var Q17;
            {var subQ0=sQuery(id+"F28.wireOp",EDGE,"E121.MirrorCS");Q17=makeQuery(id+"F28.imprint","IMPRINT",FACE,{"disambiguationData":[TD([[makeQuery(id+"F28.imprint","IMPRINT",EDGE,{"derivedFrom":subQ0}),-1.0]])]});}
            var Q18;
            {var subQ0=sQuery(id+"F28.wireOp",EDGE,"E122.MirrorCS");var subQ1=sQuery(id+"F28.wireOp",EDGE,"E106");var subQ2=makeQuery(id+"F28.imprint","INTERSECT",VERTEX,{"derivedFrom":[subQ1,subQ0]});Q18=makeQuery(id+"F28.imprint","IMPRINT",FACE,{"disambiguationData":[TD([[makeQuery(id+"F28.imprint","IMPRINT",EDGE,{"disambiguationData":[TD([[subQ2,1.0]])],"derivedFrom":subQ1}),1.0]])]});}
            var Q19;
            {var subQ0=sQuery(id+"F28.wireOp",EDGE,"E123.MirrorCS");Q19=makeQuery(id+"F28.imprint","IMPRINT",FACE,{"disambiguationData":[TD([[makeQuery(id+"F28.imprint","IMPRINT",EDGE,{"derivedFrom":subQ0}),-1.0]])]});}
            var Q20;
            {var subQ0=sQuery(id+"F28.wireOp",EDGE,"E119.left");var subQ1=sQuery(id+"F28.wireOp",EDGE,"E106");var subQ2=makeQuery(id+"F28.imprint","INTERSECT",VERTEX,{"derivedFrom":[subQ1,subQ0]});Q20=makeQuery(id+"F28.imprint","IMPRINT",FACE,{"disambiguationData":[TD([[makeQuery(id+"F28.imprint","IMPRINT",EDGE,{"disambiguationData":[TD([[subQ2,-1.0]])],"derivedFrom":subQ1}),1.0]])]});}
            var Q21;
            {var subQ0=sQuery(id+"F28.wireOp",EDGE,"E122.MirrorCS");var subQ1=sQuery(id+"F28.wireOp",EDGE,"E106");var subQ2=makeQuery(id+"F28.imprint","INTERSECT",VERTEX,{"derivedFrom":[subQ1,subQ0]});Q21=makeQuery(id+"F28.imprint","IMPRINT",FACE,{"disambiguationData":[TD([[makeQuery(id+"F28.imprint","IMPRINT",EDGE,{"disambiguationData":[TD([[subQ2,1.0]])],"derivedFrom":subQ1}),1.0]])]});}
            var Q22;
            {var subQ0=sQuery(id+"F28.wireOp",EDGE,"E121.MirrorCS");Q22=makeQuery(id+"F28.imprint","IMPRINT",FACE,{"disambiguationData":[TD([[makeQuery(id+"F28.imprint","IMPRINT",EDGE,{"derivedFrom":subQ0}),-1.0]])]});}
            var Q23;
            {var subQ0=sQuery(id+"F28.wireOp",EDGE,"E119.left");var subQ1=sQuery(id+"F28.wireOp",EDGE,"E106");var subQ2=makeQuery(id+"F28.imprint","INTERSECT",VERTEX,{"derivedFrom":[subQ1,subQ0]});Q23=makeQuery(id+"F28.imprint","IMPRINT",FACE,{"disambiguationData":[TD([[makeQuery(id+"F28.imprint","IMPRINT",EDGE,{"disambiguationData":[TD([[subQ2,-1.0]])],"derivedFrom":subQ1}),1.0]])]});}
            var Q24;
            {var subQ0=sQuery(id+"F28.wireOp",EDGE,"E122.MirrorCS");var subQ1=sQuery(id+"F28.wireOp",EDGE,"E106");var subQ2=makeQuery(id+"F28.imprint","INTERSECT",VERTEX,{"derivedFrom":[subQ1,subQ0]});Q24=makeQuery(id+"F28.imprint","IMPRINT",FACE,{"disambiguationData":[TD([[makeQuery(id+"F28.imprint","IMPRINT",EDGE,{"disambiguationData":[TD([[subQ2,1.0]])],"derivedFrom":subQ1}),1.0]])]});}
            var Q25;
            {var subQ0=sQuery(id+"F28.wireOp",EDGE,"E119.left");var subQ1=sQuery(id+"F28.wireOp",EDGE,"E106");var subQ2=makeQuery(id+"F28.imprint","INTERSECT",VERTEX,{"derivedFrom":[subQ1,subQ0]});Q25=makeQuery(id+"F28.imprint","IMPRINT",FACE,{"disambiguationData":[TD([[makeQuery(id+"F28.imprint","IMPRINT",EDGE,{"disambiguationData":[TD([[subQ2,-1.0]])],"derivedFrom":subQ1}),1.0]])]});}
            var Q26;
            {var subQ0=sQuery(id+"F28.wireOp",EDGE,"E122.MirrorCS");var subQ1=sQuery(id+"F28.wireOp",EDGE,"E106");var subQ2=makeQuery(id+"F28.imprint","INTERSECT",VERTEX,{"derivedFrom":[subQ1,subQ0]});Q26=makeQuery(id+"F28.imprint","IMPRINT",FACE,{"disambiguationData":[TD([[makeQuery(id+"F28.imprint","IMPRINT",EDGE,{"disambiguationData":[TD([[subQ2,1.0]])],"derivedFrom":subQ1}),1.0]])]});}
            var Q27;
            {var subQ0=sQuery(id+"F28.wireOp",EDGE,"E119.left");var subQ1=sQuery(id+"F28.wireOp",EDGE,"E106");var subQ2=makeQuery(id+"F28.imprint","INTERSECT",VERTEX,{"derivedFrom":[subQ1,subQ0]});Q27=makeQuery(id+"F28.imprint","IMPRINT",FACE,{"disambiguationData":[TD([[makeQuery(id+"F28.imprint","IMPRINT",EDGE,{"disambiguationData":[TD([[subQ2,-1.0]])],"derivedFrom":subQ1}),1.0]])]});}
            var Q28;
            {var subQ0=sQuery(id+"F28.wireOp",EDGE,"E119.left");var subQ1=sQuery(id+"F28.wireOp",EDGE,"E106");var subQ2=makeQuery(id+"F28.imprint","INTERSECT",VERTEX,{"derivedFrom":[subQ1,subQ0]});Q28=makeQuery(id+"F28.imprint","IMPRINT",FACE,{"disambiguationData":[TD([[makeQuery(id+"F28.imprint","IMPRINT",EDGE,{"disambiguationData":[TD([[subQ2,-1.0]])],"derivedFrom":subQ1}),1.0]])]});}
            var Q29;
            {var subQ0=sQuery(id+"F28.wireOp",EDGE,"E122.MirrorCS");var subQ1=sQuery(id+"F28.wireOp",EDGE,"E106");var subQ2=makeQuery(id+"F28.imprint","INTERSECT",VERTEX,{"derivedFrom":[subQ1,subQ0]});Q29=makeQuery(id+"F28.imprint","IMPRINT",FACE,{"disambiguationData":[TD([[makeQuery(id+"F28.imprint","IMPRINT",EDGE,{"disambiguationData":[TD([[subQ2,1.0]])],"derivedFrom":subQ1}),1.0]])]});}
            var Q30;
            {var subQ1=sQuery(id+"F28.wireOp",EDGE,"E119.bottom");Q30=makeQuery(id+"F28.imprint","IMPRINT",FACE,{"disambiguationData":[TD([[makeQuery(id+"F28.imprint","IMPRINT",EDGE,{"derivedFrom":subQ1}),-1.0]])]});}
            var Q31;
            {var subQ1=sQuery(id+"F28.wireOp",EDGE,"E119.bottom");Q31=makeQuery(id+"F28.imprint","IMPRINT",FACE,{"disambiguationData":[TD([[makeQuery(id+"F28.imprint","IMPRINT",EDGE,{"derivedFrom":subQ1}),-1.0]])]});}
            extrude(context, id + "F33", {"entities" : qUnion([Q0, Q1, Q2, Q3, Q4, Q5, Q6, Q7, Q8, Q9, Q10, Q11, Q12, Q13, Q14, Q15, Q16, Q17, Q18, Q19, Q20, Q21, Q22, Q23, Q24, Q25, Q26, Q27, Q28, Q29, Q30, Q31]), "depth" : 25.4 * mm});
        }
        {
            var Q0;
            {var subQ0=sQuery(id+"F28.wireOp",EDGE,"E126.MirrorCS");var subQ1=sQuery(id+"F28.wireOp",EDGE,"E111.MirrorCS");var subQ2=makeQuery(id+"F28.imprint","INTERSECT",VERTEX,{"derivedFrom":[subQ1,subQ0]});Q0=makeQuery(id+"F28.imprint","IMPRINT",FACE,{"disambiguationData":[TD([[makeQuery(id+"F28.imprint","IMPRINT",EDGE,{"disambiguationData":[TD([[subQ2,1.0]])],"derivedFrom":subQ1}),-1.0]])]});}
            var Q1;
            {var subQ0=sQuery(id+"F28.wireOp",EDGE,"E129.MirrorCS");var subQ1=sQuery(id+"F28.wireOp",EDGE,"E111.MirrorCS");var subQ2=makeQuery(id+"F28.imprint","INTERSECT",VERTEX,{"derivedFrom":[subQ1,subQ0]});Q1=makeQuery(id+"F28.imprint","IMPRINT",FACE,{"disambiguationData":[TD([[makeQuery(id+"F28.imprint","IMPRINT",EDGE,{"disambiguationData":[TD([[subQ2,-1.0]])],"derivedFrom":subQ1}),-1.0]])]});}
            var Q2;
            {var subQ0=sQuery(id+"F28.wireOp",EDGE,"E119.left");var subQ1=sQuery(id+"F28.wireOp",EDGE,"XHsj2Bdy-5fj5-9Be5-5Zvq-8SLI1EAt6y1m");var subQ2=makeQuery(id+"F28.imprint","INTERSECT",VERTEX,{"derivedFrom":[subQ1,subQ0]});Q2=makeQuery(id+"F28.imprint","IMPRINT",FACE,{"disambiguationData":[TD([[makeQuery(id+"F28.imprint","IMPRINT",EDGE,{"disambiguationData":[TD([[subQ2,1.0]])],"derivedFrom":subQ1}),-1.0]])]});}
            var Q3;
            {var subQ0=sQuery(id+"F28.wireOp",EDGE,"E119.left");var subQ1=sQuery(id+"F28.wireOp",EDGE,"XHsj2Bdy-5fj5-9Be5-5Zvq-8SLI1EAt6y1m");var subQ2=makeQuery(id+"F28.imprint","INTERSECT",VERTEX,{"derivedFrom":[subQ1,subQ0]});Q3=makeQuery(id+"F28.imprint","IMPRINT",FACE,{"disambiguationData":[TD([[makeQuery(id+"F28.imprint","IMPRINT",EDGE,{"disambiguationData":[TD([[subQ2,1.0]])],"derivedFrom":subQ1}),1.0]])]});}
            var Q4;
            {var subQ0=sQuery(id+"F28.wireOp",EDGE,"E122.MirrorCS");var subQ1=sQuery(id+"F28.wireOp",EDGE,"E106");var subQ2=makeQuery(id+"F28.imprint","INTERSECT",VERTEX,{"derivedFrom":[subQ1,subQ0]});Q4=makeQuery(id+"F28.imprint","IMPRINT",FACE,{"disambiguationData":[TD([[makeQuery(id+"F28.imprint","IMPRINT",EDGE,{"disambiguationData":[TD([[subQ2,1.0]])],"derivedFrom":subQ1}),1.0]])]});}
            extrude(context, id + "F34", {"entities" : qUnion([Q0, Q1, Q2, Q3, Q4]), "operationType" : NewBodyOperationType.ADD, "oppositeDirection" : true, "depth" : 1.65 * mm});
        }
        {
            var Q0;
            Q0=makeQuery(id+"F9.imprint","IMPRINT",FACE,{"disambiguationData":[TD([[makeQuery(id+"F9.imprint","IMPRINT",EDGE,{"derivedFrom":sQuery(id+"F9.wireOp",EDGE,"E49.9.0.0")}),1.0]])]});
            var Q1;
            Q1=makeQuery(id+"F9.imprint","IMPRINT",FACE,{"disambiguationData":[TD([[makeQuery(id+"F9.imprint","IMPRINT",EDGE,{"derivedFrom":sQuery(id+"F9.wireOp",EDGE,"E49.9.6.0")}),1.0]])]});
            var Q2;
            Q2=makeQuery(id+"F9.imprint","IMPRINT",FACE,{"disambiguationData":[TD([[makeQuery(id+"F9.imprint","IMPRINT",EDGE,{"derivedFrom":sQuery(id+"F9.wireOp",EDGE,"E49.5.6.0")}),1.0]])]});
            var Q3;
            Q3=makeQuery(id+"F9.imprint","IMPRINT",FACE,{"disambiguationData":[TD([[makeQuery(id+"F9.imprint","IMPRINT",EDGE,{"derivedFrom":sQuery(id+"F9.wireOp",EDGE,"E49.5.0.0")}),1.0]])]});
            extrude(context, id + "F35", {"entities" : qUnion([Q0, Q1, Q2, Q3]), "operationType" : NewBodyOperationType.REMOVE, "depth" : 76.2 * mm});
        }
        {
            var Q0;
            Q0=makeQuery(id+"F33.opExtrude","CAP_FACE",FACE,{"disambiguationData":[OSD([sQuery(id+"F28.wireOp",EDGE,"E119.bottom"),sQuery(id+"F28.wireOp",EDGE,"E119.top"),sQuery(id+"F28.wireOp",EDGE,"E119.left"),sQuery(id+"F28.wireOp",EDGE,"E119.right"),sQuery(id+"F28.wireOp",EDGE,"E133"),sQuery(id+"F28.wireOp",EDGE,"E140")])],"isStart":false});
            var sketch = newSketch(context, id + "F36", { "sketchPlane" : qUnion([Q0])});
            skCircle(sketch, "E155", {"center": v(25.4, 152.4) * mm, "radius": 7.62 * mm});
            skCircle(sketch, "E156", {"center": v(43.4, 139.7) * mm, "radius": 7.62 * mm});
            skCircle(sketch, "E157", {"center": v(43.4, 88.9) * mm, "radius": 7.62 * mm});
            skLineSegment(sketch, "E158", {"start": v(12.7, 114.3) * mm, "end": v(127, 114.3) * mm});
            skLineSegment(sketch, "E159", {"start": v(127, 114.3) * mm, "end": v(127, 0) * mm});
            skCircle(sketch, "E160.MirrorC", {"center": v(210.6, 88.9) * mm, "radius": 7.62 * mm});
            skCircle(sketch, "E161.MirrorC", {"center": v(210.6, 139.7) * mm, "radius": 7.62 * mm});
            skCircle(sketch, "E162.MirrorC", {"center": v(228.6, 152.4) * mm, "radius": 7.62 * mm});
            skLineSegment(sketch, "E163", {"start": v(127, 0) * mm, "end": v(12.7, 0) * mm});
            skCircle(sketch, "E164.MirrorC", {"center": v(43.4, -88.9) * mm, "radius": 7.62 * mm});
            skCircle(sketch, "E165.MirrorC", {"center": v(43.4, -139.7) * mm, "radius": 7.62 * mm});
            skCircle(sketch, "E166.MirrorC", {"center": v(25.4, -152.4) * mm, "radius": 7.62 * mm});
            skCircle(sketch, "E167.MirrorC", {"center": v(210.6, -88.9) * mm, "radius": 7.62 * mm});
            skCircle(sketch, "E168.MirrorC", {"center": v(210.6, -139.7) * mm, "radius": 7.62 * mm});
            skCircle(sketch, "E169.MirrorC", {"center": v(228.6, -152.4) * mm, "radius": 7.62 * mm});
            skSolve(sketch);
        }
        {
            var Q0;
            Q0 = qSketchRegion(id + "F36", true);
            extrude(context, id + "F37", {"entities" : qUnion([Q0]), "operationType" : NewBodyOperationType.REMOVE, "oppositeDirection" : true, "depth" : 10.16 * mm});
        }
        {
            var Q0;
            Q0=makeQuery(id+"F28.imprint","IMPRINT",FACE,{"disambiguationData":[TD([[makeQuery(id+"F28.imprint","IMPRINT",EDGE,{"derivedFrom":sQuery(id+"F28.wireOp",EDGE,"E141")}),1.0]])]});
            var Q1;
            Q1=makeQuery(id+"F28.imprint","IMPRINT",FACE,{"disambiguationData":[TD([[makeQuery(id+"F28.imprint","IMPRINT",EDGE,{"derivedFrom":sQuery(id+"F28.wireOp",EDGE,"E144")}),1.0]])]});
            var Q2;
            Q2=makeQuery(id+"F28.imprint","IMPRINT",FACE,{"disambiguationData":[TD([[makeQuery(id+"F28.imprint","IMPRINT",EDGE,{"derivedFrom":sQuery(id+"F28.wireOp",EDGE,"E142")}),1.0]])]});
            var Q3;
            Q3=makeQuery(id+"F28.imprint","IMPRINT",FACE,{"disambiguationData":[TD([[makeQuery(id+"F28.imprint","IMPRINT",EDGE,{"derivedFrom":sQuery(id+"F28.wireOp",EDGE,"E143")}),1.0]])]});
            var Q4;
            Q4=makeQuery(id+"F28.imprint","IMPRINT",FACE,{"disambiguationData":[TD([[makeQuery(id+"F28.imprint","IMPRINT",EDGE,{"derivedFrom":sQuery(id+"F28.wireOp",EDGE,"E148")}),1.0]])]});
            var Q5;
            Q5=makeQuery(id+"F28.imprint","IMPRINT",FACE,{"disambiguationData":[TD([[makeQuery(id+"F28.imprint","IMPRINT",EDGE,{"derivedFrom":sQuery(id+"F28.wireOp",EDGE,"E147")}),1.0]])]});
            var Q6;
            Q6=makeQuery(id+"F28.imprint","IMPRINT",FACE,{"disambiguationData":[TD([[makeQuery(id+"F28.imprint","IMPRINT",EDGE,{"derivedFrom":sQuery(id+"F28.wireOp",EDGE,"E145")}),1.0]])]});
            var Q7;
            Q7=makeQuery(id+"F28.imprint","IMPRINT",FACE,{"disambiguationData":[TD([[makeQuery(id+"F28.imprint","IMPRINT",EDGE,{"derivedFrom":sQuery(id+"F28.wireOp",EDGE,"E146")}),1.0]])]});
            var Q8;
            Q8=sQuery(id+"F28.wireOp",EDGE,"E144");
            var Q9;
            Q9=sQuery(id+"F28.wireOp",EDGE,"E141");
            var Q10;
            Q10=sQuery(id+"F28.wireOp",EDGE,"E143");
            var Q11;
            Q11=sQuery(id+"F28.wireOp",EDGE,"E142");
            var Q12;
            Q12=sQuery(id+"F28.wireOp",EDGE,"E148");
            var Q13;
            Q13=sQuery(id+"F28.wireOp",EDGE,"E147");
            var Q14;
            Q14=sQuery(id+"F28.wireOp",EDGE,"E145");
            var Q15;
            Q15=sQuery(id+"F28.wireOp",EDGE,"E146");
            extrude(context, id + "F38", {"entities" : qUnion([Q0, Q1, Q2, Q3, Q4, Q5, Q6, Q7]), "operationType" : NewBodyOperationType.REMOVE, "surfaceEntities" : qUnion([Q8, Q9, Q10, Q11, Q12, Q13, Q14, Q15]), "oppositeDirection" : true, "depth" : 19.05 * mm});
        }
        {
            var Q0;
            Q0=qCreatedBy(makeId("Front.planeOp"),FACE);
            cPlane(context, id + "F39", {"entities" : qUnion([Q0]), "cplaneType" : CPlaneType.OFFSET, "offset" : 76.2 * mm, "width" : 152.4 * mm, "height" : 152.4 * mm});
        }
        {
            var Q0;
            Q0=qCreatedBy(id+"F39.planeOp",FACE);
            var sketch = newSketch(context, id + "F40", { "sketchPlane" : qUnion([Q0])});
            skLineSegment(sketch, "E170", {"start": v(0, 0) * mm, "end": v(241.3, 0) * mm});
            skCircle(sketch, "E171", {"center": v(241.3, 0) * mm, "radius": 15.88 * mm});
            skLineSegment(sketch, "E172", {"start": v(0, 0) * mm, "end": v(-241.3, 0) * mm});
            skLineSegment(sketch, "E173", {"start": v(0, 0) * mm, "end": v(-12.7, 0) * mm});
            skLineSegment(sketch, "E174", {"start": v(0, 0) * mm, "end": v(12.7, 0) * mm});
            skCircle(sketch, "E175", {"center": v(12.7, 0) * mm, "radius": 15.88 * mm});
            skCircle(sketch, "E176", {"center": v(-12.7, 0) * mm, "radius": 15.88 * mm});
            skCircle(sketch, "E177", {"center": v(-241.3, 0) * mm, "radius": 15.88 * mm});
            skSolve(sketch);
        }
        {
            var Q0;
            Q0 = qSketchRegion(id + "F40", true);
            extrude(context, id + "F41", {"entities" : qUnion([Q0]), "operationType" : NewBodyOperationType.REMOVE, "oppositeDirection" : true, "depth" : 152.4 * mm});
        }
        {
            var Q0;
            Q0=qCreatedBy(makeId("Right.planeOp"),FACE);
            cPlane(context, id + "F42", {"entities" : qUnion([Q0]), "cplaneType" : CPlaneType.OFFSET, "offset" : 203.2 * mm, "width" : 152.4 * mm, "height" : 152.4 * mm});
        }
        {
            var Q0;
            Q0=qCreatedBy(makeId("Right.planeOp"),FACE);
            cPlane(context, id + "F43", {"entities" : qUnion([Q0]), "cplaneType" : CPlaneType.OFFSET, "offset" : 203.2 * mm, "oppositeDirection" : true, "width" : 152.4 * mm, "height" : 152.4 * mm});
        }
        {
            var Q0;
            Q0=qCreatedBy(id+"F42.planeOp",FACE);
            var sketch = newSketch(context, id + "F44", { "sketchPlane" : qUnion([Q0])});
            skLineSegment(sketch, "E178", {"start": v(0, 0) * mm, "end": v(-165.1, 0) * mm});
            skLineSegment(sketch, "E179", {"start": v(0, 0) * mm, "end": v(165.1, 0) * mm});
            skCircle(sketch, "E180", {"center": v(165.1, 0) * mm, "radius": 15.88 * mm});
            skCircle(sketch, "E181", {"center": v(-165.1, 0) * mm, "radius": 15.88 * mm});
            skSolve(sketch);
        }
        {
            var Q0;
            Q0 = qSketchRegion(id + "F44", true);
            extrude(context, id + "F45", {"entities" : qUnion([Q0]), "operationType" : NewBodyOperationType.REMOVE, "oppositeDirection" : true, "depth" : 152.4 * mm});
        }
        {
            var Q0;
            Q0=qCreatedBy(id+"F43.planeOp",FACE);
            var sketch = newSketch(context, id + "F46", { "sketchPlane" : qUnion([Q0])});
            skLineSegment(sketch, "E182", {"start": v(0, 0) * mm, "end": v(165.1, 0) * mm});
            skLineSegment(sketch, "E183", {"start": v(0, 0) * mm, "end": v(-165.1, 0) * mm});
            skCircle(sketch, "E184", {"center": v(-165.1, 0) * mm, "radius": 15.88 * mm});
            skCircle(sketch, "E185", {"center": v(165.1, 0) * mm, "radius": 15.88 * mm});
            skSolve(sketch);
        }
        {
            var Q0;
            Q0 = qSketchRegion(id + "F46", true);
            extrude(context, id + "F47", {"entities" : qUnion([Q0]), "operationType" : NewBodyOperationType.REMOVE, "depth" : 152.4 * mm});
        }
        {
            var Q0;
            Q0=makeQuery(id+"F41.boolean.opBoolean","COPY",EDGE,{"derivedFrom":makeQuery(id+"F41.opExtrude","CAP_EDGE",EDGE,{"disambiguationData":[OSD([sQuery(id+"F40.wireOp",EDGE,"E171")])],"isStart":false})});
            var Q1;
            Q1=makeQuery(id+"F41.boolean.opBoolean","COPY",EDGE,{"derivedFrom":makeQuery(id+"F41.opExtrude","CAP_EDGE",EDGE,{"disambiguationData":[OSD([sQuery(id+"F40.wireOp",EDGE,"E171")])],"isStart":true})});
            var Q2;
            Q2=makeQuery(id+"F41.boolean.opBoolean","COPY",EDGE,{"derivedFrom":makeQuery(id+"F41.opExtrude","CAP_EDGE",EDGE,{"disambiguationData":[OSD([sQuery(id+"F40.wireOp",EDGE,"E175")])],"isStart":false})});
            var Q3;
            Q3=makeQuery(id+"F41.boolean.opBoolean","COPY",EDGE,{"derivedFrom":makeQuery(id+"F41.opExtrude","CAP_EDGE",EDGE,{"disambiguationData":[OSD([sQuery(id+"F40.wireOp",EDGE,"E175")])],"isStart":true})});
            var Q4;
            Q4=makeQuery(id+"F41.boolean.opBoolean","COPY",EDGE,{"derivedFrom":makeQuery(id+"F41.opExtrude","CAP_EDGE",EDGE,{"disambiguationData":[OSD([sQuery(id+"F40.wireOp",EDGE,"E176")])],"isStart":true})});
            var Q5;
            Q5=makeQuery(id+"F41.boolean.opBoolean","COPY",EDGE,{"derivedFrom":makeQuery(id+"F41.opExtrude","CAP_EDGE",EDGE,{"disambiguationData":[OSD([sQuery(id+"F40.wireOp",EDGE,"E176")])],"isStart":false})});
            var Q6;
            Q6=makeQuery(id+"F41.boolean.opBoolean","COPY",EDGE,{"derivedFrom":makeQuery(id+"F41.opExtrude","CAP_EDGE",EDGE,{"disambiguationData":[OSD([sQuery(id+"F40.wireOp",EDGE,"E177")])],"isStart":false})});
            var Q7;
            Q7=makeQuery(id+"F41.boolean.opBoolean","COPY",EDGE,{"derivedFrom":makeQuery(id+"F41.opExtrude","CAP_EDGE",EDGE,{"disambiguationData":[OSD([sQuery(id+"F40.wireOp",EDGE,"E177")])],"isStart":true})});
            var Q8;
            Q8=makeQuery(id+"F47.boolean.opBoolean","COPY",EDGE,{"derivedFrom":makeQuery(id+"F47.opExtrude","CAP_EDGE",EDGE,{"disambiguationData":[OSD([sQuery(id+"F46.wireOp",EDGE,"E185")])],"isStart":false})});
            var Q9;
            Q9=makeQuery(id+"F47.boolean.opBoolean","COPY",EDGE,{"derivedFrom":makeQuery(id+"F47.opExtrude","CAP_EDGE",EDGE,{"disambiguationData":[OSD([sQuery(id+"F46.wireOp",EDGE,"E185")])],"isStart":true})});
            var Q10;
            Q10=makeQuery(id+"F47.boolean.opBoolean","COPY",EDGE,{"derivedFrom":makeQuery(id+"F47.opExtrude","CAP_EDGE",EDGE,{"disambiguationData":[OSD([sQuery(id+"F46.wireOp",EDGE,"E184")])],"isStart":false})});
            var Q11;
            Q11=makeQuery(id+"F47.boolean.opBoolean","COPY",EDGE,{"derivedFrom":makeQuery(id+"F47.opExtrude","CAP_EDGE",EDGE,{"disambiguationData":[OSD([sQuery(id+"F46.wireOp",EDGE,"E184")])],"isStart":true})});
            var Q12;
            Q12=makeQuery(id+"F45.boolean.opBoolean","COPY",EDGE,{"derivedFrom":makeQuery(id+"F45.opExtrude","CAP_EDGE",EDGE,{"disambiguationData":[OSD([sQuery(id+"F44.wireOp",EDGE,"E181")])],"isStart":false})});
            var Q13;
            Q13=makeQuery(id+"F45.boolean.opBoolean","COPY",EDGE,{"derivedFrom":makeQuery(id+"F45.opExtrude","CAP_EDGE",EDGE,{"disambiguationData":[OSD([sQuery(id+"F44.wireOp",EDGE,"E181")])],"isStart":true})});
            var Q14;
            Q14=makeQuery(id+"F45.boolean.opBoolean","COPY",EDGE,{"derivedFrom":makeQuery(id+"F45.opExtrude","CAP_EDGE",EDGE,{"disambiguationData":[OSD([sQuery(id+"F44.wireOp",EDGE,"E180")])],"isStart":true})});
            var Q15;
            Q15=makeQuery(id+"F45.boolean.opBoolean","COPY",EDGE,{"derivedFrom":makeQuery(id+"F45.opExtrude","CAP_EDGE",EDGE,{"disambiguationData":[OSD([sQuery(id+"F44.wireOp",EDGE,"E180")])],"isStart":false})});
            fillet(context, id + "F48", {"entities" : qUnion([Q0, Q1, Q2, Q3, Q4, Q5, Q6, Q7, Q8, Q9, Q10, Q11, Q12, Q13, Q14, Q15]), "radius" : 15.88 * mm, "tangentPropagation" : true, "allowEdgeOverflow" : false});
        }
        {
            var Q0;
            Q0=makeQuery(id+"F48.opFillet","BLEND_EDGE",EDGE,{"blendedFrom":[makeQuery(id+"F41.boolean.opBoolean","COPY",EDGE,{"derivedFrom":makeQuery(id+"F41.opExtrude","CAP_EDGE",EDGE,{"disambiguationData":[OSD([sQuery(id+"F40.wireOp",EDGE,"E171")])],"isStart":false})}),makeQuery(id+"F12.opExtrude","CAP_FACE",FACE,{"disambiguationData":[OSD([sQuery(id+"F11.wireOp",EDGE,"E59.MirrorCS"),sQuery(id+"F11.wireOp",EDGE,"E60.MirrorCS"),sQuery(id+"F11.wireOp",EDGE,"E61.MirrorCS"),sQuery(id+"F11.wireOp",EDGE,"E62")])],"isStart":true})],"blendedInto":[makeQuery(id+"F12.opExtrude","CAP_FACE",FACE,{"disambiguationData":[OSD([sQuery(id+"F11.wireOp",EDGE,"E59.MirrorCS"),sQuery(id+"F11.wireOp",EDGE,"E60.MirrorCS"),sQuery(id+"F11.wireOp",EDGE,"E61.MirrorCS"),sQuery(id+"F11.wireOp",EDGE,"E62")])],"isStart":true})]});
            var Q1;
            Q1=makeQuery(id+"F48.opFillet","BLEND_EDGE",EDGE,{"blendedFrom":[makeQuery(id+"F41.boolean.opBoolean","COPY",EDGE,{"derivedFrom":makeQuery(id+"F41.opExtrude","CAP_EDGE",EDGE,{"disambiguationData":[OSD([sQuery(id+"F40.wireOp",EDGE,"E171")])],"isStart":true})}),makeQuery(id+"F12.opExtrude","SWEPT_FACE",FACE,{"disambiguationData":[OSD([sQuery(id+"F11.wireOp",EDGE,"E60.MirrorCS")])]})],"blendedInto":[makeQuery(id+"F12.opExtrude","SWEPT_FACE",FACE,{"disambiguationData":[OSD([sQuery(id+"F11.wireOp",EDGE,"E60.MirrorCS")])]})]});
            var Q2;
            Q2=makeQuery(id+"F48.opFillet","BLEND_EDGE",EDGE,{"blendedFrom":[makeQuery(id+"F41.boolean.opBoolean","COPY",EDGE,{"derivedFrom":makeQuery(id+"F41.opExtrude","CAP_EDGE",EDGE,{"disambiguationData":[OSD([sQuery(id+"F40.wireOp",EDGE,"E175")])],"isStart":false})}),makeQuery(id+"F12.opExtrude","CAP_FACE",FACE,{"disambiguationData":[OSD([sQuery(id+"F11.wireOp",EDGE,"E59.MirrorCS"),sQuery(id+"F11.wireOp",EDGE,"E60.MirrorCS"),sQuery(id+"F11.wireOp",EDGE,"E61.MirrorCS"),sQuery(id+"F11.wireOp",EDGE,"E62")])],"isStart":true})],"blendedInto":[makeQuery(id+"F12.opExtrude","CAP_FACE",FACE,{"disambiguationData":[OSD([sQuery(id+"F11.wireOp",EDGE,"E59.MirrorCS"),sQuery(id+"F11.wireOp",EDGE,"E60.MirrorCS"),sQuery(id+"F11.wireOp",EDGE,"E61.MirrorCS"),sQuery(id+"F11.wireOp",EDGE,"E62")])],"isStart":true})]});
            var Q3;
            Q3=makeQuery(id+"F41.boolean.opBoolean","INTERSECT",EDGE,{"derivedFrom":[makeQuery(id+"F12.opExtrude","SWEPT_FACE",FACE,{"disambiguationData":[OSD([sQuery(id+"F11.wireOp",EDGE,"E62")])]}),makeQuery(id+"F41.opExtrude","SWEPT_FACE",FACE,{"disambiguationData":[OSD([sQuery(id+"F40.wireOp",EDGE,"E175")])]})]});
            var Q4;
            Q4=makeQuery(id+"F41.boolean.opBoolean","INTERSECT",EDGE,{"derivedFrom":[makeQuery(id+"F12.opExtrude","CAP_FACE",FACE,{"disambiguationData":[OSD([sQuery(id+"F11.wireOp",EDGE,"E54"),sQuery(id+"F11.wireOp",EDGE,"E56"),sQuery(id+"F11.wireOp",EDGE,"E57"),sQuery(id+"F11.wireOp",EDGE,"E58"),sQuery(id+"F11.wireOp",EDGE,"E63")])],"isStart":true}),makeQuery(id+"F41.opExtrude","SWEPT_FACE",FACE,{"disambiguationData":[OSD([sQuery(id+"F40.wireOp",EDGE,"E176")])]})]});
            var Q5;
            Q5=makeQuery(id+"F48.opFillet","BLEND_EDGE",EDGE,{"blendedFrom":[makeQuery(id+"F41.boolean.opBoolean","COPY",EDGE,{"derivedFrom":makeQuery(id+"F41.opExtrude","CAP_EDGE",EDGE,{"disambiguationData":[OSD([sQuery(id+"F40.wireOp",EDGE,"E176")])],"isStart":true})}),makeQuery(id+"F12.opExtrude","SWEPT_FACE",FACE,{"disambiguationData":[OSD([sQuery(id+"F11.wireOp",EDGE,"E54")])]})],"blendedInto":[makeQuery(id+"F12.opExtrude","SWEPT_FACE",FACE,{"disambiguationData":[OSD([sQuery(id+"F11.wireOp",EDGE,"E54")])]})]});
            var Q6;
            Q6=makeQuery(id+"F41.boolean.opBoolean","INTERSECT",EDGE,{"derivedFrom":[makeQuery(id+"F12.opExtrude","CAP_FACE",FACE,{"disambiguationData":[OSD([sQuery(id+"F11.wireOp",EDGE,"E54"),sQuery(id+"F11.wireOp",EDGE,"E56"),sQuery(id+"F11.wireOp",EDGE,"E57"),sQuery(id+"F11.wireOp",EDGE,"E58"),sQuery(id+"F11.wireOp",EDGE,"E63")])],"isStart":true}),makeQuery(id+"F41.opExtrude","SWEPT_FACE",FACE,{"disambiguationData":[OSD([sQuery(id+"F40.wireOp",EDGE,"E177")])]})]});
            var Q7;
            Q7=makeQuery(id+"F48.opFillet","BLEND_EDGE",EDGE,{"blendedFrom":[makeQuery(id+"F41.boolean.opBoolean","COPY",EDGE,{"derivedFrom":makeQuery(id+"F41.opExtrude","CAP_EDGE",EDGE,{"disambiguationData":[OSD([sQuery(id+"F40.wireOp",EDGE,"E177")])],"isStart":true})}),makeQuery(id+"F12.opExtrude","SWEPT_FACE",FACE,{"disambiguationData":[OSD([sQuery(id+"F11.wireOp",EDGE,"E57")])]})],"blendedInto":[makeQuery(id+"F12.opExtrude","SWEPT_FACE",FACE,{"disambiguationData":[OSD([sQuery(id+"F11.wireOp",EDGE,"E57")])]})]});
            var Q8;
            Q8=makeQuery(id+"F45.boolean.opBoolean","INTERSECT",EDGE,{"derivedFrom":[makeQuery(id+"F12.opExtrude","CAP_FACE",FACE,{"disambiguationData":[OSD([sQuery(id+"F11.wireOp",EDGE,"E59.MirrorCS"),sQuery(id+"F11.wireOp",EDGE,"E60.MirrorCS"),sQuery(id+"F11.wireOp",EDGE,"E61.MirrorCS"),sQuery(id+"F11.wireOp",EDGE,"E62")])],"isStart":true}),makeQuery(id+"F45.opExtrude","SWEPT_FACE",FACE,{"disambiguationData":[OSD([sQuery(id+"F44.wireOp",EDGE,"E180")])]})]});
            var Q9;
            Q9=makeQuery(id+"F45.boolean.opBoolean","INTERSECT",EDGE,{"derivedFrom":[makeQuery(id+"F12.opExtrude","SWEPT_FACE",FACE,{"disambiguationData":[OSD([sQuery(id+"F11.wireOp",EDGE,"E59.MirrorCS")])]}),makeQuery(id+"F45.opExtrude","SWEPT_FACE",FACE,{"disambiguationData":[OSD([sQuery(id+"F44.wireOp",EDGE,"E180")])]})]});
            var Q10;
            Q10=makeQuery(id+"F47.boolean.opBoolean","INTERSECT",EDGE,{"derivedFrom":[makeQuery(id+"F12.opExtrude","SWEPT_FACE",FACE,{"disambiguationData":[OSD([sQuery(id+"F11.wireOp",EDGE,"E56")])]}),makeQuery(id+"F47.opExtrude","SWEPT_FACE",FACE,{"disambiguationData":[OSD([sQuery(id+"F46.wireOp",EDGE,"E185")])]})]});
            var Q11;
            Q11=makeQuery(id+"F48.opFillet","BLEND_EDGE",EDGE,{"blendedFrom":[makeQuery(id+"F47.boolean.opBoolean","COPY",EDGE,{"derivedFrom":makeQuery(id+"F47.opExtrude","CAP_EDGE",EDGE,{"disambiguationData":[OSD([sQuery(id+"F46.wireOp",EDGE,"E185")])],"isStart":false})}),makeQuery(id+"F12.opExtrude","CAP_FACE",FACE,{"disambiguationData":[OSD([sQuery(id+"F11.wireOp",EDGE,"E54"),sQuery(id+"F11.wireOp",EDGE,"E56"),sQuery(id+"F11.wireOp",EDGE,"E57"),sQuery(id+"F11.wireOp",EDGE,"E58"),sQuery(id+"F11.wireOp",EDGE,"E63")])],"isStart":true})],"blendedInto":[makeQuery(id+"F12.opExtrude","CAP_FACE",FACE,{"disambiguationData":[OSD([sQuery(id+"F11.wireOp",EDGE,"E54"),sQuery(id+"F11.wireOp",EDGE,"E56"),sQuery(id+"F11.wireOp",EDGE,"E57"),sQuery(id+"F11.wireOp",EDGE,"E58"),sQuery(id+"F11.wireOp",EDGE,"E63")])],"isStart":true})]});
            var Q12;
            Q12=makeQuery(id+"F47.boolean.opBoolean","INTERSECT",EDGE,{"derivedFrom":[makeQuery(id+"F12.opExtrude","CAP_FACE",FACE,{"disambiguationData":[OSD([sQuery(id+"F11.wireOp",EDGE,"E54"),sQuery(id+"F11.wireOp",EDGE,"E56"),sQuery(id+"F11.wireOp",EDGE,"E57"),sQuery(id+"F11.wireOp",EDGE,"E58"),sQuery(id+"F11.wireOp",EDGE,"E63")])],"isStart":true}),makeQuery(id+"F47.opExtrude","SWEPT_FACE",FACE,{"disambiguationData":[OSD([sQuery(id+"F46.wireOp",EDGE,"E184")])]})]});
            var Q13;
            Q13=makeQuery(id+"F47.boolean.opBoolean","INTERSECT",EDGE,{"derivedFrom":[makeQuery(id+"F12.opExtrude","SWEPT_FACE",FACE,{"disambiguationData":[OSD([sQuery(id+"F11.wireOp",EDGE,"E58"),sQuery(id+"F11.wireOp",EDGE,"E63")])]}),makeQuery(id+"F47.opExtrude","SWEPT_FACE",FACE,{"disambiguationData":[OSD([sQuery(id+"F46.wireOp",EDGE,"E184")])]})]});
            var Q14;
            Q14=makeQuery(id+"F45.boolean.opBoolean","INTERSECT",EDGE,{"derivedFrom":[makeQuery(id+"F12.opExtrude","CAP_FACE",FACE,{"disambiguationData":[OSD([sQuery(id+"F11.wireOp",EDGE,"E59.MirrorCS"),sQuery(id+"F11.wireOp",EDGE,"E60.MirrorCS"),sQuery(id+"F11.wireOp",EDGE,"E61.MirrorCS"),sQuery(id+"F11.wireOp",EDGE,"E62")])],"isStart":true}),makeQuery(id+"F45.opExtrude","SWEPT_FACE",FACE,{"disambiguationData":[OSD([sQuery(id+"F44.wireOp",EDGE,"E181")])]})]});
            var Q15;
            Q15=makeQuery(id+"F45.boolean.opBoolean","INTERSECT",EDGE,{"derivedFrom":[makeQuery(id+"F12.opExtrude","SWEPT_FACE",FACE,{"disambiguationData":[OSD([sQuery(id+"F11.wireOp",EDGE,"E61.MirrorCS")])]}),makeQuery(id+"F45.opExtrude","SWEPT_FACE",FACE,{"disambiguationData":[OSD([sQuery(id+"F44.wireOp",EDGE,"E181")])]})]});
            fillet(context, id + "F49", {"entities" : qUnion([Q0, Q1, Q2, Q3, Q4, Q5, Q6, Q7, Q8, Q9, Q10, Q11, Q12, Q13, Q14, Q15]), "radius" : 5.08 * mm, "tangentPropagation" : true, "allowEdgeOverflow" : false});
        }
    });
